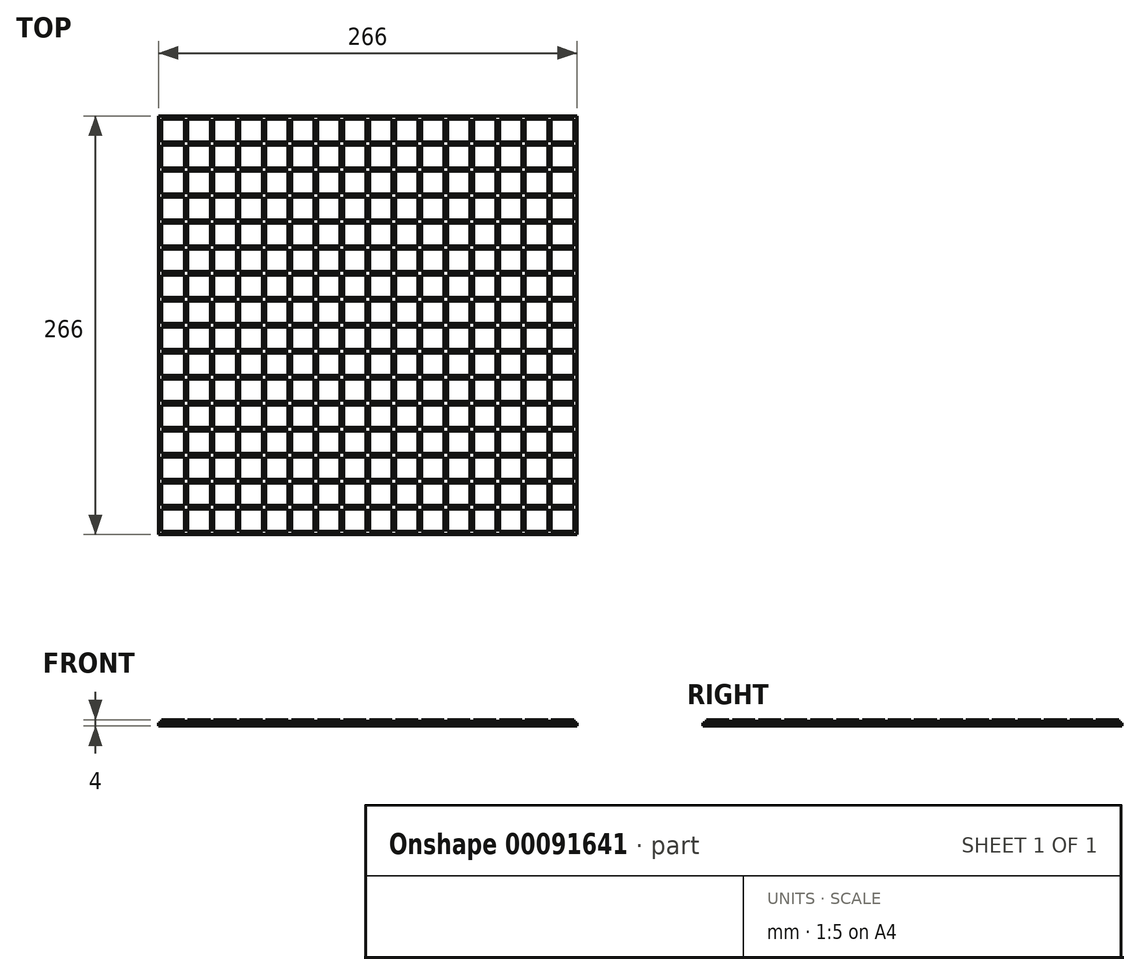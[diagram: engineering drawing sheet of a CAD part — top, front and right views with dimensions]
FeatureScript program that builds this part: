
annotation { "Feature Type Name" : "Feature", "Feature Type Description" : "" }
export const myFeature = defineFeature(function(context is Context, id is Id, definition is map)
    precondition{}
    {
        {
            var Q0;
            Q0=qCreatedBy(makeId("Top.planeOp"),FACE);
            var sketch = newSketch(context, id + "F0", { "sketchPlane" : qUnion([Q0])});
            skLineSegment(sketch, "E0.bottom", {"start": v(133, 133) * mm, "end": v(-133, 133) * mm});
            skLineSegment(sketch, "E0.top", {"start": v(133, -133) * mm, "end": v(-133, -133) * mm});
            skLineSegment(sketch, "E0.left", {"start": v(133, 133) * mm, "end": v(133, -133) * mm});
            skLineSegment(sketch, "E0.right", {"start": v(-133, 133) * mm, "end": v(-133, -133) * mm});
            skPoint(sketch, "E0.middle", {"position": v(0, 0) * mm});
            skSolve(sketch);
        }
        {
            var Q0;
            Q0=qCreatedBy(makeId("Top.planeOp"),FACE);
            var sketch = newSketch(context, id + "F1", { "sketchPlane" : qUnion([Q0])});
            skLineSegment(sketch, "E1.bottom", {"start": v(-116.5, 131) * mm, "end": v(-131, 131) * mm});
            skLineSegment(sketch, "E1.top", {"start": v(-116.5, 116.5) * mm, "end": v(-131, 116.5) * mm});
            skLineSegment(sketch, "E1.left", {"start": v(-116.5, 131) * mm, "end": v(-116.5, 116.5) * mm});
            skLineSegment(sketch, "E1.right", {"start": v(-131, 131) * mm, "end": v(-131, 116.5) * mm});
            skPoint(sketch, "E1.middle", {"position": v(-123.75, 123.75) * mm});
            skPoint(sketch, "E2.0.1.0", {"position": v(-123.75, 107.25) * mm});
            skLineSegment(sketch, "E2.0.1.1", {"start": v(-131, 114.5) * mm, "end": v(-131, 100) * mm});
            skLineSegment(sketch, "E2.0.1.2", {"start": v(-116.5, 114.5) * mm, "end": v(-116.5, 100) * mm});
            skLineSegment(sketch, "E2.0.1.3", {"start": v(-116.5, 100) * mm, "end": v(-131, 100) * mm});
            skLineSegment(sketch, "E2.0.1.4", {"start": v(-116.5, 114.5) * mm, "end": v(-131, 114.5) * mm});
            skPoint(sketch, "E2.0.2.0", {"position": v(-123.75, 90.75) * mm});
            skLineSegment(sketch, "E2.0.2.1", {"start": v(-131, 98) * mm, "end": v(-131, 83.5) * mm});
            skLineSegment(sketch, "E2.0.2.2", {"start": v(-116.5, 98) * mm, "end": v(-116.5, 83.5) * mm});
            skLineSegment(sketch, "E2.0.2.3", {"start": v(-116.5, 83.5) * mm, "end": v(-131, 83.5) * mm});
            skLineSegment(sketch, "E2.0.2.4", {"start": v(-116.5, 98) * mm, "end": v(-131, 98) * mm});
            skPoint(sketch, "E2.0.3.0", {"position": v(-123.75, 74.25) * mm});
            skLineSegment(sketch, "E2.0.3.1", {"start": v(-131, 81.5) * mm, "end": v(-131, 67) * mm});
            skLineSegment(sketch, "E2.0.3.2", {"start": v(-116.5, 81.5) * mm, "end": v(-116.5, 67) * mm});
            skLineSegment(sketch, "E2.0.3.3", {"start": v(-116.5, 67) * mm, "end": v(-131, 67) * mm});
            skLineSegment(sketch, "E2.0.3.4", {"start": v(-116.5, 81.5) * mm, "end": v(-131, 81.5) * mm});
            skPoint(sketch, "E2.0.4.0", {"position": v(-123.75, 57.75) * mm});
            skLineSegment(sketch, "E2.0.4.1", {"start": v(-131, 65) * mm, "end": v(-131, 50.5) * mm});
            skLineSegment(sketch, "E2.0.4.2", {"start": v(-116.5, 65) * mm, "end": v(-116.5, 50.5) * mm});
            skLineSegment(sketch, "E2.0.4.3", {"start": v(-116.5, 50.5) * mm, "end": v(-131, 50.5) * mm});
            skLineSegment(sketch, "E2.0.4.4", {"start": v(-116.5, 65) * mm, "end": v(-131, 65) * mm});
            skPoint(sketch, "E2.0.5.0", {"position": v(-123.75, 41.25) * mm});
            skLineSegment(sketch, "E2.0.5.1", {"start": v(-131, 48.5) * mm, "end": v(-131, 34) * mm});
            skLineSegment(sketch, "E2.0.5.2", {"start": v(-116.5, 48.5) * mm, "end": v(-116.5, 34) * mm});
            skLineSegment(sketch, "E2.0.5.3", {"start": v(-116.5, 34) * mm, "end": v(-131, 34) * mm});
            skLineSegment(sketch, "E2.0.5.4", {"start": v(-116.5, 48.5) * mm, "end": v(-131, 48.5) * mm});
            skPoint(sketch, "E2.0.6.0", {"position": v(-123.75, 24.75) * mm});
            skLineSegment(sketch, "E2.0.6.1", {"start": v(-131, 32) * mm, "end": v(-131, 17.5) * mm});
            skLineSegment(sketch, "E2.0.6.2", {"start": v(-116.5, 32) * mm, "end": v(-116.5, 17.5) * mm});
            skLineSegment(sketch, "E2.0.6.3", {"start": v(-116.5, 17.5) * mm, "end": v(-131, 17.5) * mm});
            skLineSegment(sketch, "E2.0.6.4", {"start": v(-116.5, 32) * mm, "end": v(-131, 32) * mm});
            skPoint(sketch, "E2.0.7.0", {"position": v(-123.75, 8.25) * mm});
            skLineSegment(sketch, "E2.0.7.1", {"start": v(-131, 15.5) * mm, "end": v(-131, 1) * mm});
            skLineSegment(sketch, "E2.0.7.2", {"start": v(-116.5, 15.5) * mm, "end": v(-116.5, 1) * mm});
            skLineSegment(sketch, "E2.0.7.3", {"start": v(-116.5, 1) * mm, "end": v(-131, 1) * mm});
            skLineSegment(sketch, "E2.0.7.4", {"start": v(-116.5, 15.5) * mm, "end": v(-131, 15.5) * mm});
            skPoint(sketch, "E2.0.8.0", {"position": v(-123.75, -8.25) * mm});
            skLineSegment(sketch, "E2.0.8.1", {"start": v(-131, -1) * mm, "end": v(-131, -15.5) * mm});
            skLineSegment(sketch, "E2.0.8.2", {"start": v(-116.5, -1) * mm, "end": v(-116.5, -15.5) * mm});
            skLineSegment(sketch, "E2.0.8.3", {"start": v(-116.5, -15.5) * mm, "end": v(-131, -15.5) * mm});
            skLineSegment(sketch, "E2.0.8.4", {"start": v(-116.5, -1) * mm, "end": v(-131, -1) * mm});
            skPoint(sketch, "E2.0.9.0", {"position": v(-123.75, -24.75) * mm});
            skLineSegment(sketch, "E2.0.9.1", {"start": v(-131, -17.5) * mm, "end": v(-131, -32) * mm});
            skLineSegment(sketch, "E2.0.9.2", {"start": v(-116.5, -17.5) * mm, "end": v(-116.5, -32) * mm});
            skLineSegment(sketch, "E2.0.9.3", {"start": v(-116.5, -32) * mm, "end": v(-131, -32) * mm});
            skLineSegment(sketch, "E2.0.9.4", {"start": v(-116.5, -17.5) * mm, "end": v(-131, -17.5) * mm});
            skPoint(sketch, "E2.0.10.0", {"position": v(-123.75, -41.25) * mm});
            skLineSegment(sketch, "E2.0.10.1", {"start": v(-131, -34) * mm, "end": v(-131, -48.5) * mm});
            skLineSegment(sketch, "E2.0.10.2", {"start": v(-116.5, -34) * mm, "end": v(-116.5, -48.5) * mm});
            skLineSegment(sketch, "E2.0.10.3", {"start": v(-116.5, -48.5) * mm, "end": v(-131, -48.5) * mm});
            skLineSegment(sketch, "E2.0.10.4", {"start": v(-116.5, -34) * mm, "end": v(-131, -34) * mm});
            skPoint(sketch, "E2.0.11.0", {"position": v(-123.75, -57.75) * mm});
            skLineSegment(sketch, "E2.0.11.1", {"start": v(-131, -50.5) * mm, "end": v(-131, -65) * mm});
            skLineSegment(sketch, "E2.0.11.2", {"start": v(-116.5, -50.5) * mm, "end": v(-116.5, -65) * mm});
            skLineSegment(sketch, "E2.0.11.3", {"start": v(-116.5, -65) * mm, "end": v(-131, -65) * mm});
            skLineSegment(sketch, "E2.0.11.4", {"start": v(-116.5, -50.5) * mm, "end": v(-131, -50.5) * mm});
            skPoint(sketch, "E2.0.12.0", {"position": v(-123.75, -74.25) * mm});
            skLineSegment(sketch, "E2.0.12.1", {"start": v(-131, -67) * mm, "end": v(-131, -81.5) * mm});
            skLineSegment(sketch, "E2.0.12.2", {"start": v(-116.5, -67) * mm, "end": v(-116.5, -81.5) * mm});
            skLineSegment(sketch, "E2.0.12.3", {"start": v(-116.5, -81.5) * mm, "end": v(-131, -81.5) * mm});
            skLineSegment(sketch, "E2.0.12.4", {"start": v(-116.5, -67) * mm, "end": v(-131, -67) * mm});
            skPoint(sketch, "E2.0.13.0", {"position": v(-123.75, -90.75) * mm});
            skLineSegment(sketch, "E2.0.13.1", {"start": v(-131, -83.5) * mm, "end": v(-131, -98) * mm});
            skLineSegment(sketch, "E2.0.13.2", {"start": v(-116.5, -83.5) * mm, "end": v(-116.5, -98) * mm});
            skLineSegment(sketch, "E2.0.13.3", {"start": v(-116.5, -98) * mm, "end": v(-131, -98) * mm});
            skLineSegment(sketch, "E2.0.13.4", {"start": v(-116.5, -83.5) * mm, "end": v(-131, -83.5) * mm});
            skPoint(sketch, "E2.0.14.0", {"position": v(-123.75, -107.25) * mm});
            skLineSegment(sketch, "E2.0.14.1", {"start": v(-131, -100) * mm, "end": v(-131, -114.5) * mm});
            skLineSegment(sketch, "E2.0.14.2", {"start": v(-116.5, -100) * mm, "end": v(-116.5, -114.5) * mm});
            skLineSegment(sketch, "E2.0.14.3", {"start": v(-116.5, -114.5) * mm, "end": v(-131, -114.5) * mm});
            skLineSegment(sketch, "E2.0.14.4", {"start": v(-116.5, -100) * mm, "end": v(-131, -100) * mm});
            skPoint(sketch, "E2.0.15.0", {"position": v(-123.75, -123.75) * mm});
            skLineSegment(sketch, "E2.0.15.1", {"start": v(-131, -116.5) * mm, "end": v(-131, -131) * mm});
            skLineSegment(sketch, "E2.0.15.2", {"start": v(-116.5, -116.5) * mm, "end": v(-116.5, -131) * mm});
            skLineSegment(sketch, "E2.0.15.3", {"start": v(-116.5, -131) * mm, "end": v(-131, -131) * mm});
            skLineSegment(sketch, "E2.0.15.4", {"start": v(-116.5, -116.5) * mm, "end": v(-131, -116.5) * mm});
            skPoint(sketch, "E2.1.0.0", {"position": v(-107.25, 123.75) * mm});
            skLineSegment(sketch, "E2.1.0.1", {"start": v(-114.5, 131) * mm, "end": v(-114.5, 116.5) * mm});
            skLineSegment(sketch, "E2.1.0.2", {"start": v(-100, 131) * mm, "end": v(-100, 116.5) * mm});
            skLineSegment(sketch, "E2.1.0.3", {"start": v(-100, 116.5) * mm, "end": v(-114.5, 116.5) * mm});
            skLineSegment(sketch, "E2.1.0.4", {"start": v(-100, 131) * mm, "end": v(-114.5, 131) * mm});
            skPoint(sketch, "E2.1.1.0", {"position": v(-107.25, 107.25) * mm});
            skLineSegment(sketch, "E2.1.1.1", {"start": v(-114.5, 114.5) * mm, "end": v(-114.5, 100) * mm});
            skLineSegment(sketch, "E2.1.1.2", {"start": v(-100, 114.5) * mm, "end": v(-100, 100) * mm});
            skLineSegment(sketch, "E2.1.1.3", {"start": v(-100, 100) * mm, "end": v(-114.5, 100) * mm});
            skLineSegment(sketch, "E2.1.1.4", {"start": v(-100, 114.5) * mm, "end": v(-114.5, 114.5) * mm});
            skPoint(sketch, "E2.1.2.0", {"position": v(-107.25, 90.75) * mm});
            skLineSegment(sketch, "E2.1.2.1", {"start": v(-114.5, 98) * mm, "end": v(-114.5, 83.5) * mm});
            skLineSegment(sketch, "E2.1.2.2", {"start": v(-100, 98) * mm, "end": v(-100, 83.5) * mm});
            skLineSegment(sketch, "E2.1.2.3", {"start": v(-100, 83.5) * mm, "end": v(-114.5, 83.5) * mm});
            skLineSegment(sketch, "E2.1.2.4", {"start": v(-100, 98) * mm, "end": v(-114.5, 98) * mm});
            skPoint(sketch, "E2.1.3.0", {"position": v(-107.25, 74.25) * mm});
            skLineSegment(sketch, "E2.1.3.1", {"start": v(-114.5, 81.5) * mm, "end": v(-114.5, 67) * mm});
            skLineSegment(sketch, "E2.1.3.2", {"start": v(-100, 81.5) * mm, "end": v(-100, 67) * mm});
            skLineSegment(sketch, "E2.1.3.3", {"start": v(-100, 67) * mm, "end": v(-114.5, 67) * mm});
            skLineSegment(sketch, "E2.1.3.4", {"start": v(-100, 81.5) * mm, "end": v(-114.5, 81.5) * mm});
            skPoint(sketch, "E2.1.4.0", {"position": v(-107.25, 57.75) * mm});
            skLineSegment(sketch, "E2.1.4.1", {"start": v(-114.5, 65) * mm, "end": v(-114.5, 50.5) * mm});
            skLineSegment(sketch, "E2.1.4.2", {"start": v(-100, 65) * mm, "end": v(-100, 50.5) * mm});
            skLineSegment(sketch, "E2.1.4.3", {"start": v(-100, 50.5) * mm, "end": v(-114.5, 50.5) * mm});
            skLineSegment(sketch, "E2.1.4.4", {"start": v(-100, 65) * mm, "end": v(-114.5, 65) * mm});
            skPoint(sketch, "E2.1.5.0", {"position": v(-107.25, 41.25) * mm});
            skLineSegment(sketch, "E2.1.5.1", {"start": v(-114.5, 48.5) * mm, "end": v(-114.5, 34) * mm});
            skLineSegment(sketch, "E2.1.5.2", {"start": v(-100, 48.5) * mm, "end": v(-100, 34) * mm});
            skLineSegment(sketch, "E2.1.5.3", {"start": v(-100, 34) * mm, "end": v(-114.5, 34) * mm});
            skLineSegment(sketch, "E2.1.5.4", {"start": v(-100, 48.5) * mm, "end": v(-114.5, 48.5) * mm});
            skPoint(sketch, "E2.1.6.0", {"position": v(-107.25, 24.75) * mm});
            skLineSegment(sketch, "E2.1.6.1", {"start": v(-114.5, 32) * mm, "end": v(-114.5, 17.5) * mm});
            skLineSegment(sketch, "E2.1.6.2", {"start": v(-100, 32) * mm, "end": v(-100, 17.5) * mm});
            skLineSegment(sketch, "E2.1.6.3", {"start": v(-100, 17.5) * mm, "end": v(-114.5, 17.5) * mm});
            skLineSegment(sketch, "E2.1.6.4", {"start": v(-100, 32) * mm, "end": v(-114.5, 32) * mm});
            skPoint(sketch, "E2.1.7.0", {"position": v(-107.25, 8.25) * mm});
            skLineSegment(sketch, "E2.1.7.1", {"start": v(-114.5, 15.5) * mm, "end": v(-114.5, 1) * mm});
            skLineSegment(sketch, "E2.1.7.2", {"start": v(-100, 15.5) * mm, "end": v(-100, 1) * mm});
            skLineSegment(sketch, "E2.1.7.3", {"start": v(-100, 1) * mm, "end": v(-114.5, 1) * mm});
            skLineSegment(sketch, "E2.1.7.4", {"start": v(-100, 15.5) * mm, "end": v(-114.5, 15.5) * mm});
            skPoint(sketch, "E2.1.8.0", {"position": v(-107.25, -8.25) * mm});
            skLineSegment(sketch, "E2.1.8.1", {"start": v(-114.5, -1) * mm, "end": v(-114.5, -15.5) * mm});
            skLineSegment(sketch, "E2.1.8.2", {"start": v(-100, -1) * mm, "end": v(-100, -15.5) * mm});
            skLineSegment(sketch, "E2.1.8.3", {"start": v(-100, -15.5) * mm, "end": v(-114.5, -15.5) * mm});
            skLineSegment(sketch, "E2.1.8.4", {"start": v(-100, -1) * mm, "end": v(-114.5, -1) * mm});
            skPoint(sketch, "E2.1.9.0", {"position": v(-107.25, -24.75) * mm});
            skLineSegment(sketch, "E2.1.9.1", {"start": v(-114.5, -17.5) * mm, "end": v(-114.5, -32) * mm});
            skLineSegment(sketch, "E2.1.9.2", {"start": v(-100, -17.5) * mm, "end": v(-100, -32) * mm});
            skLineSegment(sketch, "E2.1.9.3", {"start": v(-100, -32) * mm, "end": v(-114.5, -32) * mm});
            skLineSegment(sketch, "E2.1.9.4", {"start": v(-100, -17.5) * mm, "end": v(-114.5, -17.5) * mm});
            skPoint(sketch, "E2.1.10.0", {"position": v(-107.25, -41.25) * mm});
            skLineSegment(sketch, "E2.1.10.1", {"start": v(-114.5, -34) * mm, "end": v(-114.5, -48.5) * mm});
            skLineSegment(sketch, "E2.1.10.2", {"start": v(-100, -34) * mm, "end": v(-100, -48.5) * mm});
            skLineSegment(sketch, "E2.1.10.3", {"start": v(-100, -48.5) * mm, "end": v(-114.5, -48.5) * mm});
            skLineSegment(sketch, "E2.1.10.4", {"start": v(-100, -34) * mm, "end": v(-114.5, -34) * mm});
            skPoint(sketch, "E2.1.11.0", {"position": v(-107.25, -57.75) * mm});
            skLineSegment(sketch, "E2.1.11.1", {"start": v(-114.5, -50.5) * mm, "end": v(-114.5, -65) * mm});
            skLineSegment(sketch, "E2.1.11.2", {"start": v(-100, -50.5) * mm, "end": v(-100, -65) * mm});
            skLineSegment(sketch, "E2.1.11.3", {"start": v(-100, -65) * mm, "end": v(-114.5, -65) * mm});
            skLineSegment(sketch, "E2.1.11.4", {"start": v(-100, -50.5) * mm, "end": v(-114.5, -50.5) * mm});
            skPoint(sketch, "E2.1.12.0", {"position": v(-107.25, -74.25) * mm});
            skLineSegment(sketch, "E2.1.12.1", {"start": v(-114.5, -67) * mm, "end": v(-114.5, -81.5) * mm});
            skLineSegment(sketch, "E2.1.12.2", {"start": v(-100, -67) * mm, "end": v(-100, -81.5) * mm});
            skLineSegment(sketch, "E2.1.12.3", {"start": v(-100, -81.5) * mm, "end": v(-114.5, -81.5) * mm});
            skLineSegment(sketch, "E2.1.12.4", {"start": v(-100, -67) * mm, "end": v(-114.5, -67) * mm});
            skPoint(sketch, "E2.1.13.0", {"position": v(-107.25, -90.75) * mm});
            skLineSegment(sketch, "E2.1.13.1", {"start": v(-114.5, -83.5) * mm, "end": v(-114.5, -98) * mm});
            skLineSegment(sketch, "E2.1.13.2", {"start": v(-100, -83.5) * mm, "end": v(-100, -98) * mm});
            skLineSegment(sketch, "E2.1.13.3", {"start": v(-100, -98) * mm, "end": v(-114.5, -98) * mm});
            skLineSegment(sketch, "E2.1.13.4", {"start": v(-100, -83.5) * mm, "end": v(-114.5, -83.5) * mm});
            skPoint(sketch, "E2.1.14.0", {"position": v(-107.25, -107.25) * mm});
            skLineSegment(sketch, "E2.1.14.1", {"start": v(-114.5, -100) * mm, "end": v(-114.5, -114.5) * mm});
            skLineSegment(sketch, "E2.1.14.2", {"start": v(-100, -100) * mm, "end": v(-100, -114.5) * mm});
            skLineSegment(sketch, "E2.1.14.3", {"start": v(-100, -114.5) * mm, "end": v(-114.5, -114.5) * mm});
            skLineSegment(sketch, "E2.1.14.4", {"start": v(-100, -100) * mm, "end": v(-114.5, -100) * mm});
            skPoint(sketch, "E2.1.15.0", {"position": v(-107.25, -123.75) * mm});
            skLineSegment(sketch, "E2.1.15.1", {"start": v(-114.5, -116.5) * mm, "end": v(-114.5, -131) * mm});
            skLineSegment(sketch, "E2.1.15.2", {"start": v(-100, -116.5) * mm, "end": v(-100, -131) * mm});
            skLineSegment(sketch, "E2.1.15.3", {"start": v(-100, -131) * mm, "end": v(-114.5, -131) * mm});
            skLineSegment(sketch, "E2.1.15.4", {"start": v(-100, -116.5) * mm, "end": v(-114.5, -116.5) * mm});
            skPoint(sketch, "E2.2.0.0", {"position": v(-90.75, 123.75) * mm});
            skLineSegment(sketch, "E2.2.0.1", {"start": v(-98, 131) * mm, "end": v(-98, 116.5) * mm});
            skLineSegment(sketch, "E2.2.0.2", {"start": v(-83.5, 131) * mm, "end": v(-83.5, 116.5) * mm});
            skLineSegment(sketch, "E2.2.0.3", {"start": v(-83.5, 116.5) * mm, "end": v(-98, 116.5) * mm});
            skLineSegment(sketch, "E2.2.0.4", {"start": v(-83.5, 131) * mm, "end": v(-98, 131) * mm});
            skPoint(sketch, "E2.2.1.0", {"position": v(-90.75, 107.25) * mm});
            skLineSegment(sketch, "E2.2.1.1", {"start": v(-98, 114.5) * mm, "end": v(-98, 100) * mm});
            skLineSegment(sketch, "E2.2.1.2", {"start": v(-83.5, 114.5) * mm, "end": v(-83.5, 100) * mm});
            skLineSegment(sketch, "E2.2.1.3", {"start": v(-83.5, 100) * mm, "end": v(-98, 100) * mm});
            skLineSegment(sketch, "E2.2.1.4", {"start": v(-83.5, 114.5) * mm, "end": v(-98, 114.5) * mm});
            skPoint(sketch, "E2.2.2.0", {"position": v(-90.75, 90.75) * mm});
            skLineSegment(sketch, "E2.2.2.1", {"start": v(-98, 98) * mm, "end": v(-98, 83.5) * mm});
            skLineSegment(sketch, "E2.2.2.2", {"start": v(-83.5, 98) * mm, "end": v(-83.5, 83.5) * mm});
            skLineSegment(sketch, "E2.2.2.3", {"start": v(-83.5, 83.5) * mm, "end": v(-98, 83.5) * mm});
            skLineSegment(sketch, "E2.2.2.4", {"start": v(-83.5, 98) * mm, "end": v(-98, 98) * mm});
            skPoint(sketch, "E2.2.3.0", {"position": v(-90.75, 74.25) * mm});
            skLineSegment(sketch, "E2.2.3.1", {"start": v(-98, 81.5) * mm, "end": v(-98, 67) * mm});
            skLineSegment(sketch, "E2.2.3.2", {"start": v(-83.5, 81.5) * mm, "end": v(-83.5, 67) * mm});
            skLineSegment(sketch, "E2.2.3.3", {"start": v(-83.5, 67) * mm, "end": v(-98, 67) * mm});
            skLineSegment(sketch, "E2.2.3.4", {"start": v(-83.5, 81.5) * mm, "end": v(-98, 81.5) * mm});
            skPoint(sketch, "E2.2.4.0", {"position": v(-90.75, 57.75) * mm});
            skLineSegment(sketch, "E2.2.4.1", {"start": v(-98, 65) * mm, "end": v(-98, 50.5) * mm});
            skLineSegment(sketch, "E2.2.4.2", {"start": v(-83.5, 65) * mm, "end": v(-83.5, 50.5) * mm});
            skLineSegment(sketch, "E2.2.4.3", {"start": v(-83.5, 50.5) * mm, "end": v(-98, 50.5) * mm});
            skLineSegment(sketch, "E2.2.4.4", {"start": v(-83.5, 65) * mm, "end": v(-98, 65) * mm});
            skPoint(sketch, "E2.2.5.0", {"position": v(-90.75, 41.25) * mm});
            skLineSegment(sketch, "E2.2.5.1", {"start": v(-98, 48.5) * mm, "end": v(-98, 34) * mm});
            skLineSegment(sketch, "E2.2.5.2", {"start": v(-83.5, 48.5) * mm, "end": v(-83.5, 34) * mm});
            skLineSegment(sketch, "E2.2.5.3", {"start": v(-83.5, 34) * mm, "end": v(-98, 34) * mm});
            skLineSegment(sketch, "E2.2.5.4", {"start": v(-83.5, 48.5) * mm, "end": v(-98, 48.5) * mm});
            skPoint(sketch, "E2.2.6.0", {"position": v(-90.75, 24.75) * mm});
            skLineSegment(sketch, "E2.2.6.1", {"start": v(-98, 32) * mm, "end": v(-98, 17.5) * mm});
            skLineSegment(sketch, "E2.2.6.2", {"start": v(-83.5, 32) * mm, "end": v(-83.5, 17.5) * mm});
            skLineSegment(sketch, "E2.2.6.3", {"start": v(-83.5, 17.5) * mm, "end": v(-98, 17.5) * mm});
            skLineSegment(sketch, "E2.2.6.4", {"start": v(-83.5, 32) * mm, "end": v(-98, 32) * mm});
            skPoint(sketch, "E2.2.7.0", {"position": v(-90.75, 8.25) * mm});
            skLineSegment(sketch, "E2.2.7.1", {"start": v(-98, 15.5) * mm, "end": v(-98, 1) * mm});
            skLineSegment(sketch, "E2.2.7.2", {"start": v(-83.5, 15.5) * mm, "end": v(-83.5, 1) * mm});
            skLineSegment(sketch, "E2.2.7.3", {"start": v(-83.5, 1) * mm, "end": v(-98, 1) * mm});
            skLineSegment(sketch, "E2.2.7.4", {"start": v(-83.5, 15.5) * mm, "end": v(-98, 15.5) * mm});
            skPoint(sketch, "E2.2.8.0", {"position": v(-90.75, -8.25) * mm});
            skLineSegment(sketch, "E2.2.8.1", {"start": v(-98, -1) * mm, "end": v(-98, -15.5) * mm});
            skLineSegment(sketch, "E2.2.8.2", {"start": v(-83.5, -1) * mm, "end": v(-83.5, -15.5) * mm});
            skLineSegment(sketch, "E2.2.8.3", {"start": v(-83.5, -15.5) * mm, "end": v(-98, -15.5) * mm});
            skLineSegment(sketch, "E2.2.8.4", {"start": v(-83.5, -1) * mm, "end": v(-98, -1) * mm});
            skPoint(sketch, "E2.2.9.0", {"position": v(-90.75, -24.75) * mm});
            skLineSegment(sketch, "E2.2.9.1", {"start": v(-98, -17.5) * mm, "end": v(-98, -32) * mm});
            skLineSegment(sketch, "E2.2.9.2", {"start": v(-83.5, -17.5) * mm, "end": v(-83.5, -32) * mm});
            skLineSegment(sketch, "E2.2.9.3", {"start": v(-83.5, -32) * mm, "end": v(-98, -32) * mm});
            skLineSegment(sketch, "E2.2.9.4", {"start": v(-83.5, -17.5) * mm, "end": v(-98, -17.5) * mm});
            skPoint(sketch, "E2.2.10.0", {"position": v(-90.75, -41.25) * mm});
            skLineSegment(sketch, "E2.2.10.1", {"start": v(-98, -34) * mm, "end": v(-98, -48.5) * mm});
            skLineSegment(sketch, "E2.2.10.2", {"start": v(-83.5, -34) * mm, "end": v(-83.5, -48.5) * mm});
            skLineSegment(sketch, "E2.2.10.3", {"start": v(-83.5, -48.5) * mm, "end": v(-98, -48.5) * mm});
            skLineSegment(sketch, "E2.2.10.4", {"start": v(-83.5, -34) * mm, "end": v(-98, -34) * mm});
            skPoint(sketch, "E2.2.11.0", {"position": v(-90.75, -57.75) * mm});
            skLineSegment(sketch, "E2.2.11.1", {"start": v(-98, -50.5) * mm, "end": v(-98, -65) * mm});
            skLineSegment(sketch, "E2.2.11.2", {"start": v(-83.5, -50.5) * mm, "end": v(-83.5, -65) * mm});
            skLineSegment(sketch, "E2.2.11.3", {"start": v(-83.5, -65) * mm, "end": v(-98, -65) * mm});
            skLineSegment(sketch, "E2.2.11.4", {"start": v(-83.5, -50.5) * mm, "end": v(-98, -50.5) * mm});
            skPoint(sketch, "E2.2.12.0", {"position": v(-90.75, -74.25) * mm});
            skLineSegment(sketch, "E2.2.12.1", {"start": v(-98, -67) * mm, "end": v(-98, -81.5) * mm});
            skLineSegment(sketch, "E2.2.12.2", {"start": v(-83.5, -67) * mm, "end": v(-83.5, -81.5) * mm});
            skLineSegment(sketch, "E2.2.12.3", {"start": v(-83.5, -81.5) * mm, "end": v(-98, -81.5) * mm});
            skLineSegment(sketch, "E2.2.12.4", {"start": v(-83.5, -67) * mm, "end": v(-98, -67) * mm});
            skPoint(sketch, "E2.2.13.0", {"position": v(-90.75, -90.75) * mm});
            skLineSegment(sketch, "E2.2.13.1", {"start": v(-98, -83.5) * mm, "end": v(-98, -98) * mm});
            skLineSegment(sketch, "E2.2.13.2", {"start": v(-83.5, -83.5) * mm, "end": v(-83.5, -98) * mm});
            skLineSegment(sketch, "E2.2.13.3", {"start": v(-83.5, -98) * mm, "end": v(-98, -98) * mm});
            skLineSegment(sketch, "E2.2.13.4", {"start": v(-83.5, -83.5) * mm, "end": v(-98, -83.5) * mm});
            skPoint(sketch, "E2.2.14.0", {"position": v(-90.75, -107.25) * mm});
            skLineSegment(sketch, "E2.2.14.1", {"start": v(-98, -100) * mm, "end": v(-98, -114.5) * mm});
            skLineSegment(sketch, "E2.2.14.2", {"start": v(-83.5, -100) * mm, "end": v(-83.5, -114.5) * mm});
            skLineSegment(sketch, "E2.2.14.3", {"start": v(-83.5, -114.5) * mm, "end": v(-98, -114.5) * mm});
            skLineSegment(sketch, "E2.2.14.4", {"start": v(-83.5, -100) * mm, "end": v(-98, -100) * mm});
            skPoint(sketch, "E2.2.15.0", {"position": v(-90.75, -123.75) * mm});
            skLineSegment(sketch, "E2.2.15.1", {"start": v(-98, -116.5) * mm, "end": v(-98, -131) * mm});
            skLineSegment(sketch, "E2.2.15.2", {"start": v(-83.5, -116.5) * mm, "end": v(-83.5, -131) * mm});
            skLineSegment(sketch, "E2.2.15.3", {"start": v(-83.5, -131) * mm, "end": v(-98, -131) * mm});
            skLineSegment(sketch, "E2.2.15.4", {"start": v(-83.5, -116.5) * mm, "end": v(-98, -116.5) * mm});
            skPoint(sketch, "E2.3.0.0", {"position": v(-74.25, 123.75) * mm});
            skLineSegment(sketch, "E2.3.0.1", {"start": v(-81.5, 131) * mm, "end": v(-81.5, 116.5) * mm});
            skLineSegment(sketch, "E2.3.0.2", {"start": v(-67, 131) * mm, "end": v(-67, 116.5) * mm});
            skLineSegment(sketch, "E2.3.0.3", {"start": v(-67, 116.5) * mm, "end": v(-81.5, 116.5) * mm});
            skLineSegment(sketch, "E2.3.0.4", {"start": v(-67, 131) * mm, "end": v(-81.5, 131) * mm});
            skPoint(sketch, "E2.3.1.0", {"position": v(-74.25, 107.25) * mm});
            skLineSegment(sketch, "E2.3.1.1", {"start": v(-81.5, 114.5) * mm, "end": v(-81.5, 100) * mm});
            skLineSegment(sketch, "E2.3.1.2", {"start": v(-67, 114.5) * mm, "end": v(-67, 100) * mm});
            skLineSegment(sketch, "E2.3.1.3", {"start": v(-67, 100) * mm, "end": v(-81.5, 100) * mm});
            skLineSegment(sketch, "E2.3.1.4", {"start": v(-67, 114.5) * mm, "end": v(-81.5, 114.5) * mm});
            skPoint(sketch, "E2.3.2.0", {"position": v(-74.25, 90.75) * mm});
            skLineSegment(sketch, "E2.3.2.1", {"start": v(-81.5, 98) * mm, "end": v(-81.5, 83.5) * mm});
            skLineSegment(sketch, "E2.3.2.2", {"start": v(-67, 98) * mm, "end": v(-67, 83.5) * mm});
            skLineSegment(sketch, "E2.3.2.3", {"start": v(-67, 83.5) * mm, "end": v(-81.5, 83.5) * mm});
            skLineSegment(sketch, "E2.3.2.4", {"start": v(-67, 98) * mm, "end": v(-81.5, 98) * mm});
            skPoint(sketch, "E2.3.3.0", {"position": v(-74.25, 74.25) * mm});
            skLineSegment(sketch, "E2.3.3.1", {"start": v(-81.5, 81.5) * mm, "end": v(-81.5, 67) * mm});
            skLineSegment(sketch, "E2.3.3.2", {"start": v(-67, 81.5) * mm, "end": v(-67, 67) * mm});
            skLineSegment(sketch, "E2.3.3.3", {"start": v(-67, 67) * mm, "end": v(-81.5, 67) * mm});
            skLineSegment(sketch, "E2.3.3.4", {"start": v(-67, 81.5) * mm, "end": v(-81.5, 81.5) * mm});
            skPoint(sketch, "E2.3.4.0", {"position": v(-74.25, 57.75) * mm});
            skLineSegment(sketch, "E2.3.4.1", {"start": v(-81.5, 65) * mm, "end": v(-81.5, 50.5) * mm});
            skLineSegment(sketch, "E2.3.4.2", {"start": v(-67, 65) * mm, "end": v(-67, 50.5) * mm});
            skLineSegment(sketch, "E2.3.4.3", {"start": v(-67, 50.5) * mm, "end": v(-81.5, 50.5) * mm});
            skLineSegment(sketch, "E2.3.4.4", {"start": v(-67, 65) * mm, "end": v(-81.5, 65) * mm});
            skPoint(sketch, "E2.3.5.0", {"position": v(-74.25, 41.25) * mm});
            skLineSegment(sketch, "E2.3.5.1", {"start": v(-81.5, 48.5) * mm, "end": v(-81.5, 34) * mm});
            skLineSegment(sketch, "E2.3.5.2", {"start": v(-67, 48.5) * mm, "end": v(-67, 34) * mm});
            skLineSegment(sketch, "E2.3.5.3", {"start": v(-67, 34) * mm, "end": v(-81.5, 34) * mm});
            skLineSegment(sketch, "E2.3.5.4", {"start": v(-67, 48.5) * mm, "end": v(-81.5, 48.5) * mm});
            skPoint(sketch, "E2.3.6.0", {"position": v(-74.25, 24.75) * mm});
            skLineSegment(sketch, "E2.3.6.1", {"start": v(-81.5, 32) * mm, "end": v(-81.5, 17.5) * mm});
            skLineSegment(sketch, "E2.3.6.2", {"start": v(-67, 32) * mm, "end": v(-67, 17.5) * mm});
            skLineSegment(sketch, "E2.3.6.3", {"start": v(-67, 17.5) * mm, "end": v(-81.5, 17.5) * mm});
            skLineSegment(sketch, "E2.3.6.4", {"start": v(-67, 32) * mm, "end": v(-81.5, 32) * mm});
            skPoint(sketch, "E2.3.7.0", {"position": v(-74.25, 8.25) * mm});
            skLineSegment(sketch, "E2.3.7.1", {"start": v(-81.5, 15.5) * mm, "end": v(-81.5, 1) * mm});
            skLineSegment(sketch, "E2.3.7.2", {"start": v(-67, 15.5) * mm, "end": v(-67, 1) * mm});
            skLineSegment(sketch, "E2.3.7.3", {"start": v(-67, 1) * mm, "end": v(-81.5, 1) * mm});
            skLineSegment(sketch, "E2.3.7.4", {"start": v(-67, 15.5) * mm, "end": v(-81.5, 15.5) * mm});
            skPoint(sketch, "E2.3.8.0", {"position": v(-74.25, -8.25) * mm});
            skLineSegment(sketch, "E2.3.8.1", {"start": v(-81.5, -1) * mm, "end": v(-81.5, -15.5) * mm});
            skLineSegment(sketch, "E2.3.8.2", {"start": v(-67, -1) * mm, "end": v(-67, -15.5) * mm});
            skLineSegment(sketch, "E2.3.8.3", {"start": v(-67, -15.5) * mm, "end": v(-81.5, -15.5) * mm});
            skLineSegment(sketch, "E2.3.8.4", {"start": v(-67, -1) * mm, "end": v(-81.5, -1) * mm});
            skPoint(sketch, "E2.3.9.0", {"position": v(-74.25, -24.75) * mm});
            skLineSegment(sketch, "E2.3.9.1", {"start": v(-81.5, -17.5) * mm, "end": v(-81.5, -32) * mm});
            skLineSegment(sketch, "E2.3.9.2", {"start": v(-67, -17.5) * mm, "end": v(-67, -32) * mm});
            skLineSegment(sketch, "E2.3.9.3", {"start": v(-67, -32) * mm, "end": v(-81.5, -32) * mm});
            skLineSegment(sketch, "E2.3.9.4", {"start": v(-67, -17.5) * mm, "end": v(-81.5, -17.5) * mm});
            skPoint(sketch, "E2.3.10.0", {"position": v(-74.25, -41.25) * mm});
            skLineSegment(sketch, "E2.3.10.1", {"start": v(-81.5, -34) * mm, "end": v(-81.5, -48.5) * mm});
            skLineSegment(sketch, "E2.3.10.2", {"start": v(-67, -34) * mm, "end": v(-67, -48.5) * mm});
            skLineSegment(sketch, "E2.3.10.3", {"start": v(-67, -48.5) * mm, "end": v(-81.5, -48.5) * mm});
            skLineSegment(sketch, "E2.3.10.4", {"start": v(-67, -34) * mm, "end": v(-81.5, -34) * mm});
            skPoint(sketch, "E2.3.11.0", {"position": v(-74.25, -57.75) * mm});
            skLineSegment(sketch, "E2.3.11.1", {"start": v(-81.5, -50.5) * mm, "end": v(-81.5, -65) * mm});
            skLineSegment(sketch, "E2.3.11.2", {"start": v(-67, -50.5) * mm, "end": v(-67, -65) * mm});
            skLineSegment(sketch, "E2.3.11.3", {"start": v(-67, -65) * mm, "end": v(-81.5, -65) * mm});
            skLineSegment(sketch, "E2.3.11.4", {"start": v(-67, -50.5) * mm, "end": v(-81.5, -50.5) * mm});
            skPoint(sketch, "E2.3.12.0", {"position": v(-74.25, -74.25) * mm});
            skLineSegment(sketch, "E2.3.12.1", {"start": v(-81.5, -67) * mm, "end": v(-81.5, -81.5) * mm});
            skLineSegment(sketch, "E2.3.12.2", {"start": v(-67, -67) * mm, "end": v(-67, -81.5) * mm});
            skLineSegment(sketch, "E2.3.12.3", {"start": v(-67, -81.5) * mm, "end": v(-81.5, -81.5) * mm});
            skLineSegment(sketch, "E2.3.12.4", {"start": v(-67, -67) * mm, "end": v(-81.5, -67) * mm});
            skPoint(sketch, "E2.3.13.0", {"position": v(-74.25, -90.75) * mm});
            skLineSegment(sketch, "E2.3.13.1", {"start": v(-81.5, -83.5) * mm, "end": v(-81.5, -98) * mm});
            skLineSegment(sketch, "E2.3.13.2", {"start": v(-67, -83.5) * mm, "end": v(-67, -98) * mm});
            skLineSegment(sketch, "E2.3.13.3", {"start": v(-67, -98) * mm, "end": v(-81.5, -98) * mm});
            skLineSegment(sketch, "E2.3.13.4", {"start": v(-67, -83.5) * mm, "end": v(-81.5, -83.5) * mm});
            skPoint(sketch, "E2.3.14.0", {"position": v(-74.25, -107.25) * mm});
            skLineSegment(sketch, "E2.3.14.1", {"start": v(-81.5, -100) * mm, "end": v(-81.5, -114.5) * mm});
            skLineSegment(sketch, "E2.3.14.2", {"start": v(-67, -100) * mm, "end": v(-67, -114.5) * mm});
            skLineSegment(sketch, "E2.3.14.3", {"start": v(-67, -114.5) * mm, "end": v(-81.5, -114.5) * mm});
            skLineSegment(sketch, "E2.3.14.4", {"start": v(-67, -100) * mm, "end": v(-81.5, -100) * mm});
            skPoint(sketch, "E2.3.15.0", {"position": v(-74.25, -123.75) * mm});
            skLineSegment(sketch, "E2.3.15.1", {"start": v(-81.5, -116.5) * mm, "end": v(-81.5, -131) * mm});
            skLineSegment(sketch, "E2.3.15.2", {"start": v(-67, -116.5) * mm, "end": v(-67, -131) * mm});
            skLineSegment(sketch, "E2.3.15.3", {"start": v(-67, -131) * mm, "end": v(-81.5, -131) * mm});
            skLineSegment(sketch, "E2.3.15.4", {"start": v(-67, -116.5) * mm, "end": v(-81.5, -116.5) * mm});
            skPoint(sketch, "E2.4.0.0", {"position": v(-57.75, 123.75) * mm});
            skLineSegment(sketch, "E2.4.0.1", {"start": v(-65, 131) * mm, "end": v(-65, 116.5) * mm});
            skLineSegment(sketch, "E2.4.0.2", {"start": v(-50.5, 131) * mm, "end": v(-50.5, 116.5) * mm});
            skLineSegment(sketch, "E2.4.0.3", {"start": v(-50.5, 116.5) * mm, "end": v(-65, 116.5) * mm});
            skLineSegment(sketch, "E2.4.0.4", {"start": v(-50.5, 131) * mm, "end": v(-65, 131) * mm});
            skPoint(sketch, "E2.4.1.0", {"position": v(-57.75, 107.25) * mm});
            skLineSegment(sketch, "E2.4.1.1", {"start": v(-65, 114.5) * mm, "end": v(-65, 100) * mm});
            skLineSegment(sketch, "E2.4.1.2", {"start": v(-50.5, 114.5) * mm, "end": v(-50.5, 100) * mm});
            skLineSegment(sketch, "E2.4.1.3", {"start": v(-50.5, 100) * mm, "end": v(-65, 100) * mm});
            skLineSegment(sketch, "E2.4.1.4", {"start": v(-50.5, 114.5) * mm, "end": v(-65, 114.5) * mm});
            skPoint(sketch, "E2.4.2.0", {"position": v(-57.75, 90.75) * mm});
            skLineSegment(sketch, "E2.4.2.1", {"start": v(-65, 98) * mm, "end": v(-65, 83.5) * mm});
            skLineSegment(sketch, "E2.4.2.2", {"start": v(-50.5, 98) * mm, "end": v(-50.5, 83.5) * mm});
            skLineSegment(sketch, "E2.4.2.3", {"start": v(-50.5, 83.5) * mm, "end": v(-65, 83.5) * mm});
            skLineSegment(sketch, "E2.4.2.4", {"start": v(-50.5, 98) * mm, "end": v(-65, 98) * mm});
            skPoint(sketch, "E2.4.3.0", {"position": v(-57.75, 74.25) * mm});
            skLineSegment(sketch, "E2.4.3.1", {"start": v(-65, 81.5) * mm, "end": v(-65, 67) * mm});
            skLineSegment(sketch, "E2.4.3.2", {"start": v(-50.5, 81.5) * mm, "end": v(-50.5, 67) * mm});
            skLineSegment(sketch, "E2.4.3.3", {"start": v(-50.5, 67) * mm, "end": v(-65, 67) * mm});
            skLineSegment(sketch, "E2.4.3.4", {"start": v(-50.5, 81.5) * mm, "end": v(-65, 81.5) * mm});
            skPoint(sketch, "E2.4.4.0", {"position": v(-57.75, 57.75) * mm});
            skLineSegment(sketch, "E2.4.4.1", {"start": v(-65, 65) * mm, "end": v(-65, 50.5) * mm});
            skLineSegment(sketch, "E2.4.4.2", {"start": v(-50.5, 65) * mm, "end": v(-50.5, 50.5) * mm});
            skLineSegment(sketch, "E2.4.4.3", {"start": v(-50.5, 50.5) * mm, "end": v(-65, 50.5) * mm});
            skLineSegment(sketch, "E2.4.4.4", {"start": v(-50.5, 65) * mm, "end": v(-65, 65) * mm});
            skPoint(sketch, "E2.4.5.0", {"position": v(-57.75, 41.25) * mm});
            skLineSegment(sketch, "E2.4.5.1", {"start": v(-65, 48.5) * mm, "end": v(-65, 34) * mm});
            skLineSegment(sketch, "E2.4.5.2", {"start": v(-50.5, 48.5) * mm, "end": v(-50.5, 34) * mm});
            skLineSegment(sketch, "E2.4.5.3", {"start": v(-50.5, 34) * mm, "end": v(-65, 34) * mm});
            skLineSegment(sketch, "E2.4.5.4", {"start": v(-50.5, 48.5) * mm, "end": v(-65, 48.5) * mm});
            skPoint(sketch, "E2.4.6.0", {"position": v(-57.75, 24.75) * mm});
            skLineSegment(sketch, "E2.4.6.1", {"start": v(-65, 32) * mm, "end": v(-65, 17.5) * mm});
            skLineSegment(sketch, "E2.4.6.2", {"start": v(-50.5, 32) * mm, "end": v(-50.5, 17.5) * mm});
            skLineSegment(sketch, "E2.4.6.3", {"start": v(-50.5, 17.5) * mm, "end": v(-65, 17.5) * mm});
            skLineSegment(sketch, "E2.4.6.4", {"start": v(-50.5, 32) * mm, "end": v(-65, 32) * mm});
            skPoint(sketch, "E2.4.7.0", {"position": v(-57.75, 8.25) * mm});
            skLineSegment(sketch, "E2.4.7.1", {"start": v(-65, 15.5) * mm, "end": v(-65, 1) * mm});
            skLineSegment(sketch, "E2.4.7.2", {"start": v(-50.5, 15.5) * mm, "end": v(-50.5, 1) * mm});
            skLineSegment(sketch, "E2.4.7.3", {"start": v(-50.5, 1) * mm, "end": v(-65, 1) * mm});
            skLineSegment(sketch, "E2.4.7.4", {"start": v(-50.5, 15.5) * mm, "end": v(-65, 15.5) * mm});
            skPoint(sketch, "E2.4.8.0", {"position": v(-57.75, -8.25) * mm});
            skLineSegment(sketch, "E2.4.8.1", {"start": v(-65, -1) * mm, "end": v(-65, -15.5) * mm});
            skLineSegment(sketch, "E2.4.8.2", {"start": v(-50.5, -1) * mm, "end": v(-50.5, -15.5) * mm});
            skLineSegment(sketch, "E2.4.8.3", {"start": v(-50.5, -15.5) * mm, "end": v(-65, -15.5) * mm});
            skLineSegment(sketch, "E2.4.8.4", {"start": v(-50.5, -1) * mm, "end": v(-65, -1) * mm});
            skPoint(sketch, "E2.4.9.0", {"position": v(-57.75, -24.75) * mm});
            skLineSegment(sketch, "E2.4.9.1", {"start": v(-65, -17.5) * mm, "end": v(-65, -32) * mm});
            skLineSegment(sketch, "E2.4.9.2", {"start": v(-50.5, -17.5) * mm, "end": v(-50.5, -32) * mm});
            skLineSegment(sketch, "E2.4.9.3", {"start": v(-50.5, -32) * mm, "end": v(-65, -32) * mm});
            skLineSegment(sketch, "E2.4.9.4", {"start": v(-50.5, -17.5) * mm, "end": v(-65, -17.5) * mm});
            skPoint(sketch, "E2.4.10.0", {"position": v(-57.75, -41.25) * mm});
            skLineSegment(sketch, "E2.4.10.1", {"start": v(-65, -34) * mm, "end": v(-65, -48.5) * mm});
            skLineSegment(sketch, "E2.4.10.2", {"start": v(-50.5, -34) * mm, "end": v(-50.5, -48.5) * mm});
            skLineSegment(sketch, "E2.4.10.3", {"start": v(-50.5, -48.5) * mm, "end": v(-65, -48.5) * mm});
            skLineSegment(sketch, "E2.4.10.4", {"start": v(-50.5, -34) * mm, "end": v(-65, -34) * mm});
            skPoint(sketch, "E2.4.11.0", {"position": v(-57.75, -57.75) * mm});
            skLineSegment(sketch, "E2.4.11.1", {"start": v(-65, -50.5) * mm, "end": v(-65, -65) * mm});
            skLineSegment(sketch, "E2.4.11.2", {"start": v(-50.5, -50.5) * mm, "end": v(-50.5, -65) * mm});
            skLineSegment(sketch, "E2.4.11.3", {"start": v(-50.5, -65) * mm, "end": v(-65, -65) * mm});
            skLineSegment(sketch, "E2.4.11.4", {"start": v(-50.5, -50.5) * mm, "end": v(-65, -50.5) * mm});
            skPoint(sketch, "E2.4.12.0", {"position": v(-57.75, -74.25) * mm});
            skLineSegment(sketch, "E2.4.12.1", {"start": v(-65, -67) * mm, "end": v(-65, -81.5) * mm});
            skLineSegment(sketch, "E2.4.12.2", {"start": v(-50.5, -67) * mm, "end": v(-50.5, -81.5) * mm});
            skLineSegment(sketch, "E2.4.12.3", {"start": v(-50.5, -81.5) * mm, "end": v(-65, -81.5) * mm});
            skLineSegment(sketch, "E2.4.12.4", {"start": v(-50.5, -67) * mm, "end": v(-65, -67) * mm});
            skPoint(sketch, "E2.4.13.0", {"position": v(-57.75, -90.75) * mm});
            skLineSegment(sketch, "E2.4.13.1", {"start": v(-65, -83.5) * mm, "end": v(-65, -98) * mm});
            skLineSegment(sketch, "E2.4.13.2", {"start": v(-50.5, -83.5) * mm, "end": v(-50.5, -98) * mm});
            skLineSegment(sketch, "E2.4.13.3", {"start": v(-50.5, -98) * mm, "end": v(-65, -98) * mm});
            skLineSegment(sketch, "E2.4.13.4", {"start": v(-50.5, -83.5) * mm, "end": v(-65, -83.5) * mm});
            skPoint(sketch, "E2.4.14.0", {"position": v(-57.75, -107.25) * mm});
            skLineSegment(sketch, "E2.4.14.1", {"start": v(-65, -100) * mm, "end": v(-65, -114.5) * mm});
            skLineSegment(sketch, "E2.4.14.2", {"start": v(-50.5, -100) * mm, "end": v(-50.5, -114.5) * mm});
            skLineSegment(sketch, "E2.4.14.3", {"start": v(-50.5, -114.5) * mm, "end": v(-65, -114.5) * mm});
            skLineSegment(sketch, "E2.4.14.4", {"start": v(-50.5, -100) * mm, "end": v(-65, -100) * mm});
            skPoint(sketch, "E2.4.15.0", {"position": v(-57.75, -123.75) * mm});
            skLineSegment(sketch, "E2.4.15.1", {"start": v(-65, -116.5) * mm, "end": v(-65, -131) * mm});
            skLineSegment(sketch, "E2.4.15.2", {"start": v(-50.5, -116.5) * mm, "end": v(-50.5, -131) * mm});
            skLineSegment(sketch, "E2.4.15.3", {"start": v(-50.5, -131) * mm, "end": v(-65, -131) * mm});
            skLineSegment(sketch, "E2.4.15.4", {"start": v(-50.5, -116.5) * mm, "end": v(-65, -116.5) * mm});
            skPoint(sketch, "E2.5.0.0", {"position": v(-41.25, 123.75) * mm});
            skLineSegment(sketch, "E2.5.0.1", {"start": v(-48.5, 131) * mm, "end": v(-48.5, 116.5) * mm});
            skLineSegment(sketch, "E2.5.0.2", {"start": v(-34, 131) * mm, "end": v(-34, 116.5) * mm});
            skLineSegment(sketch, "E2.5.0.3", {"start": v(-34, 116.5) * mm, "end": v(-48.5, 116.5) * mm});
            skLineSegment(sketch, "E2.5.0.4", {"start": v(-34, 131) * mm, "end": v(-48.5, 131) * mm});
            skPoint(sketch, "E2.5.1.0", {"position": v(-41.25, 107.25) * mm});
            skLineSegment(sketch, "E2.5.1.1", {"start": v(-48.5, 114.5) * mm, "end": v(-48.5, 100) * mm});
            skLineSegment(sketch, "E2.5.1.2", {"start": v(-34, 114.5) * mm, "end": v(-34, 100) * mm});
            skLineSegment(sketch, "E2.5.1.3", {"start": v(-34, 100) * mm, "end": v(-48.5, 100) * mm});
            skLineSegment(sketch, "E2.5.1.4", {"start": v(-34, 114.5) * mm, "end": v(-48.5, 114.5) * mm});
            skPoint(sketch, "E2.5.2.0", {"position": v(-41.25, 90.75) * mm});
            skLineSegment(sketch, "E2.5.2.1", {"start": v(-48.5, 98) * mm, "end": v(-48.5, 83.5) * mm});
            skLineSegment(sketch, "E2.5.2.2", {"start": v(-34, 98) * mm, "end": v(-34, 83.5) * mm});
            skLineSegment(sketch, "E2.5.2.3", {"start": v(-34, 83.5) * mm, "end": v(-48.5, 83.5) * mm});
            skLineSegment(sketch, "E2.5.2.4", {"start": v(-34, 98) * mm, "end": v(-48.5, 98) * mm});
            skPoint(sketch, "E2.5.3.0", {"position": v(-41.25, 74.25) * mm});
            skLineSegment(sketch, "E2.5.3.1", {"start": v(-48.5, 81.5) * mm, "end": v(-48.5, 67) * mm});
            skLineSegment(sketch, "E2.5.3.2", {"start": v(-34, 81.5) * mm, "end": v(-34, 67) * mm});
            skLineSegment(sketch, "E2.5.3.3", {"start": v(-34, 67) * mm, "end": v(-48.5, 67) * mm});
            skLineSegment(sketch, "E2.5.3.4", {"start": v(-34, 81.5) * mm, "end": v(-48.5, 81.5) * mm});
            skPoint(sketch, "E2.5.4.0", {"position": v(-41.25, 57.75) * mm});
            skLineSegment(sketch, "E2.5.4.1", {"start": v(-48.5, 65) * mm, "end": v(-48.5, 50.5) * mm});
            skLineSegment(sketch, "E2.5.4.2", {"start": v(-34, 65) * mm, "end": v(-34, 50.5) * mm});
            skLineSegment(sketch, "E2.5.4.3", {"start": v(-34, 50.5) * mm, "end": v(-48.5, 50.5) * mm});
            skLineSegment(sketch, "E2.5.4.4", {"start": v(-34, 65) * mm, "end": v(-48.5, 65) * mm});
            skPoint(sketch, "E2.5.5.0", {"position": v(-41.25, 41.25) * mm});
            skLineSegment(sketch, "E2.5.5.1", {"start": v(-48.5, 48.5) * mm, "end": v(-48.5, 34) * mm});
            skLineSegment(sketch, "E2.5.5.2", {"start": v(-34, 48.5) * mm, "end": v(-34, 34) * mm});
            skLineSegment(sketch, "E2.5.5.3", {"start": v(-34, 34) * mm, "end": v(-48.5, 34) * mm});
            skLineSegment(sketch, "E2.5.5.4", {"start": v(-34, 48.5) * mm, "end": v(-48.5, 48.5) * mm});
            skPoint(sketch, "E2.5.6.0", {"position": v(-41.25, 24.75) * mm});
            skLineSegment(sketch, "E2.5.6.1", {"start": v(-48.5, 32) * mm, "end": v(-48.5, 17.5) * mm});
            skLineSegment(sketch, "E2.5.6.2", {"start": v(-34, 32) * mm, "end": v(-34, 17.5) * mm});
            skLineSegment(sketch, "E2.5.6.3", {"start": v(-34, 17.5) * mm, "end": v(-48.5, 17.5) * mm});
            skLineSegment(sketch, "E2.5.6.4", {"start": v(-34, 32) * mm, "end": v(-48.5, 32) * mm});
            skPoint(sketch, "E2.5.7.0", {"position": v(-41.25, 8.25) * mm});
            skLineSegment(sketch, "E2.5.7.1", {"start": v(-48.5, 15.5) * mm, "end": v(-48.5, 1) * mm});
            skLineSegment(sketch, "E2.5.7.2", {"start": v(-34, 15.5) * mm, "end": v(-34, 1) * mm});
            skLineSegment(sketch, "E2.5.7.3", {"start": v(-34, 1) * mm, "end": v(-48.5, 1) * mm});
            skLineSegment(sketch, "E2.5.7.4", {"start": v(-34, 15.5) * mm, "end": v(-48.5, 15.5) * mm});
            skPoint(sketch, "E2.5.8.0", {"position": v(-41.25, -8.25) * mm});
            skLineSegment(sketch, "E2.5.8.1", {"start": v(-48.5, -1) * mm, "end": v(-48.5, -15.5) * mm});
            skLineSegment(sketch, "E2.5.8.2", {"start": v(-34, -1) * mm, "end": v(-34, -15.5) * mm});
            skLineSegment(sketch, "E2.5.8.3", {"start": v(-34, -15.5) * mm, "end": v(-48.5, -15.5) * mm});
            skLineSegment(sketch, "E2.5.8.4", {"start": v(-34, -1) * mm, "end": v(-48.5, -1) * mm});
            skPoint(sketch, "E2.5.9.0", {"position": v(-41.25, -24.75) * mm});
            skLineSegment(sketch, "E2.5.9.1", {"start": v(-48.5, -17.5) * mm, "end": v(-48.5, -32) * mm});
            skLineSegment(sketch, "E2.5.9.2", {"start": v(-34, -17.5) * mm, "end": v(-34, -32) * mm});
            skLineSegment(sketch, "E2.5.9.3", {"start": v(-34, -32) * mm, "end": v(-48.5, -32) * mm});
            skLineSegment(sketch, "E2.5.9.4", {"start": v(-34, -17.5) * mm, "end": v(-48.5, -17.5) * mm});
            skPoint(sketch, "E2.5.10.0", {"position": v(-41.25, -41.25) * mm});
            skLineSegment(sketch, "E2.5.10.1", {"start": v(-48.5, -34) * mm, "end": v(-48.5, -48.5) * mm});
            skLineSegment(sketch, "E2.5.10.2", {"start": v(-34, -34) * mm, "end": v(-34, -48.5) * mm});
            skLineSegment(sketch, "E2.5.10.3", {"start": v(-34, -48.5) * mm, "end": v(-48.5, -48.5) * mm});
            skLineSegment(sketch, "E2.5.10.4", {"start": v(-34, -34) * mm, "end": v(-48.5, -34) * mm});
            skPoint(sketch, "E2.5.11.0", {"position": v(-41.25, -57.75) * mm});
            skLineSegment(sketch, "E2.5.11.1", {"start": v(-48.5, -50.5) * mm, "end": v(-48.5, -65) * mm});
            skLineSegment(sketch, "E2.5.11.2", {"start": v(-34, -50.5) * mm, "end": v(-34, -65) * mm});
            skLineSegment(sketch, "E2.5.11.3", {"start": v(-34, -65) * mm, "end": v(-48.5, -65) * mm});
            skLineSegment(sketch, "E2.5.11.4", {"start": v(-34, -50.5) * mm, "end": v(-48.5, -50.5) * mm});
            skPoint(sketch, "E2.5.12.0", {"position": v(-41.25, -74.25) * mm});
            skLineSegment(sketch, "E2.5.12.1", {"start": v(-48.5, -67) * mm, "end": v(-48.5, -81.5) * mm});
            skLineSegment(sketch, "E2.5.12.2", {"start": v(-34, -67) * mm, "end": v(-34, -81.5) * mm});
            skLineSegment(sketch, "E2.5.12.3", {"start": v(-34, -81.5) * mm, "end": v(-48.5, -81.5) * mm});
            skLineSegment(sketch, "E2.5.12.4", {"start": v(-34, -67) * mm, "end": v(-48.5, -67) * mm});
            skPoint(sketch, "E2.5.13.0", {"position": v(-41.25, -90.75) * mm});
            skLineSegment(sketch, "E2.5.13.1", {"start": v(-48.5, -83.5) * mm, "end": v(-48.5, -98) * mm});
            skLineSegment(sketch, "E2.5.13.2", {"start": v(-34, -83.5) * mm, "end": v(-34, -98) * mm});
            skLineSegment(sketch, "E2.5.13.3", {"start": v(-34, -98) * mm, "end": v(-48.5, -98) * mm});
            skLineSegment(sketch, "E2.5.13.4", {"start": v(-34, -83.5) * mm, "end": v(-48.5, -83.5) * mm});
            skPoint(sketch, "E2.5.14.0", {"position": v(-41.25, -107.25) * mm});
            skLineSegment(sketch, "E2.5.14.1", {"start": v(-48.5, -100) * mm, "end": v(-48.5, -114.5) * mm});
            skLineSegment(sketch, "E2.5.14.2", {"start": v(-34, -100) * mm, "end": v(-34, -114.5) * mm});
            skLineSegment(sketch, "E2.5.14.3", {"start": v(-34, -114.5) * mm, "end": v(-48.5, -114.5) * mm});
            skLineSegment(sketch, "E2.5.14.4", {"start": v(-34, -100) * mm, "end": v(-48.5, -100) * mm});
            skPoint(sketch, "E2.5.15.0", {"position": v(-41.25, -123.75) * mm});
            skLineSegment(sketch, "E2.5.15.1", {"start": v(-48.5, -116.5) * mm, "end": v(-48.5, -131) * mm});
            skLineSegment(sketch, "E2.5.15.2", {"start": v(-34, -116.5) * mm, "end": v(-34, -131) * mm});
            skLineSegment(sketch, "E2.5.15.3", {"start": v(-34, -131) * mm, "end": v(-48.5, -131) * mm});
            skLineSegment(sketch, "E2.5.15.4", {"start": v(-34, -116.5) * mm, "end": v(-48.5, -116.5) * mm});
            skPoint(sketch, "E2.6.0.0", {"position": v(-24.75, 123.75) * mm});
            skLineSegment(sketch, "E2.6.0.1", {"start": v(-32, 131) * mm, "end": v(-32, 116.5) * mm});
            skLineSegment(sketch, "E2.6.0.2", {"start": v(-17.5, 131) * mm, "end": v(-17.5, 116.5) * mm});
            skLineSegment(sketch, "E2.6.0.3", {"start": v(-17.5, 116.5) * mm, "end": v(-32, 116.5) * mm});
            skLineSegment(sketch, "E2.6.0.4", {"start": v(-17.5, 131) * mm, "end": v(-32, 131) * mm});
            skPoint(sketch, "E2.6.1.0", {"position": v(-24.75, 107.25) * mm});
            skLineSegment(sketch, "E2.6.1.1", {"start": v(-32, 114.5) * mm, "end": v(-32, 100) * mm});
            skLineSegment(sketch, "E2.6.1.2", {"start": v(-17.5, 114.5) * mm, "end": v(-17.5, 100) * mm});
            skLineSegment(sketch, "E2.6.1.3", {"start": v(-17.5, 100) * mm, "end": v(-32, 100) * mm});
            skLineSegment(sketch, "E2.6.1.4", {"start": v(-17.5, 114.5) * mm, "end": v(-32, 114.5) * mm});
            skPoint(sketch, "E2.6.2.0", {"position": v(-24.75, 90.75) * mm});
            skLineSegment(sketch, "E2.6.2.1", {"start": v(-32, 98) * mm, "end": v(-32, 83.5) * mm});
            skLineSegment(sketch, "E2.6.2.2", {"start": v(-17.5, 98) * mm, "end": v(-17.5, 83.5) * mm});
            skLineSegment(sketch, "E2.6.2.3", {"start": v(-17.5, 83.5) * mm, "end": v(-32, 83.5) * mm});
            skLineSegment(sketch, "E2.6.2.4", {"start": v(-17.5, 98) * mm, "end": v(-32, 98) * mm});
            skPoint(sketch, "E2.6.3.0", {"position": v(-24.75, 74.25) * mm});
            skLineSegment(sketch, "E2.6.3.1", {"start": v(-32, 81.5) * mm, "end": v(-32, 67) * mm});
            skLineSegment(sketch, "E2.6.3.2", {"start": v(-17.5, 81.5) * mm, "end": v(-17.5, 67) * mm});
            skLineSegment(sketch, "E2.6.3.3", {"start": v(-17.5, 67) * mm, "end": v(-32, 67) * mm});
            skLineSegment(sketch, "E2.6.3.4", {"start": v(-17.5, 81.5) * mm, "end": v(-32, 81.5) * mm});
            skPoint(sketch, "E2.6.4.0", {"position": v(-24.75, 57.75) * mm});
            skLineSegment(sketch, "E2.6.4.1", {"start": v(-32, 65) * mm, "end": v(-32, 50.5) * mm});
            skLineSegment(sketch, "E2.6.4.2", {"start": v(-17.5, 65) * mm, "end": v(-17.5, 50.5) * mm});
            skLineSegment(sketch, "E2.6.4.3", {"start": v(-17.5, 50.5) * mm, "end": v(-32, 50.5) * mm});
            skLineSegment(sketch, "E2.6.4.4", {"start": v(-17.5, 65) * mm, "end": v(-32, 65) * mm});
            skPoint(sketch, "E2.6.5.0", {"position": v(-24.75, 41.25) * mm});
            skLineSegment(sketch, "E2.6.5.1", {"start": v(-32, 48.5) * mm, "end": v(-32, 34) * mm});
            skLineSegment(sketch, "E2.6.5.2", {"start": v(-17.5, 48.5) * mm, "end": v(-17.5, 34) * mm});
            skLineSegment(sketch, "E2.6.5.3", {"start": v(-17.5, 34) * mm, "end": v(-32, 34) * mm});
            skLineSegment(sketch, "E2.6.5.4", {"start": v(-17.5, 48.5) * mm, "end": v(-32, 48.5) * mm});
            skPoint(sketch, "E2.6.6.0", {"position": v(-24.75, 24.75) * mm});
            skLineSegment(sketch, "E2.6.6.1", {"start": v(-32, 32) * mm, "end": v(-32, 17.5) * mm});
            skLineSegment(sketch, "E2.6.6.2", {"start": v(-17.5, 32) * mm, "end": v(-17.5, 17.5) * mm});
            skLineSegment(sketch, "E2.6.6.3", {"start": v(-17.5, 17.5) * mm, "end": v(-32, 17.5) * mm});
            skLineSegment(sketch, "E2.6.6.4", {"start": v(-17.5, 32) * mm, "end": v(-32, 32) * mm});
            skPoint(sketch, "E2.6.7.0", {"position": v(-24.75, 8.25) * mm});
            skLineSegment(sketch, "E2.6.7.1", {"start": v(-32, 15.5) * mm, "end": v(-32, 1) * mm});
            skLineSegment(sketch, "E2.6.7.2", {"start": v(-17.5, 15.5) * mm, "end": v(-17.5, 1) * mm});
            skLineSegment(sketch, "E2.6.7.3", {"start": v(-17.5, 1) * mm, "end": v(-32, 1) * mm});
            skLineSegment(sketch, "E2.6.7.4", {"start": v(-17.5, 15.5) * mm, "end": v(-32, 15.5) * mm});
            skPoint(sketch, "E2.6.8.0", {"position": v(-24.75, -8.25) * mm});
            skLineSegment(sketch, "E2.6.8.1", {"start": v(-32, -1) * mm, "end": v(-32, -15.5) * mm});
            skLineSegment(sketch, "E2.6.8.2", {"start": v(-17.5, -1) * mm, "end": v(-17.5, -15.5) * mm});
            skLineSegment(sketch, "E2.6.8.3", {"start": v(-17.5, -15.5) * mm, "end": v(-32, -15.5) * mm});
            skLineSegment(sketch, "E2.6.8.4", {"start": v(-17.5, -1) * mm, "end": v(-32, -1) * mm});
            skPoint(sketch, "E2.6.9.0", {"position": v(-24.75, -24.75) * mm});
            skLineSegment(sketch, "E2.6.9.1", {"start": v(-32, -17.5) * mm, "end": v(-32, -32) * mm});
            skLineSegment(sketch, "E2.6.9.2", {"start": v(-17.5, -17.5) * mm, "end": v(-17.5, -32) * mm});
            skLineSegment(sketch, "E2.6.9.3", {"start": v(-17.5, -32) * mm, "end": v(-32, -32) * mm});
            skLineSegment(sketch, "E2.6.9.4", {"start": v(-17.5, -17.5) * mm, "end": v(-32, -17.5) * mm});
            skPoint(sketch, "E2.6.10.0", {"position": v(-24.75, -41.25) * mm});
            skLineSegment(sketch, "E2.6.10.1", {"start": v(-32, -34) * mm, "end": v(-32, -48.5) * mm});
            skLineSegment(sketch, "E2.6.10.2", {"start": v(-17.5, -34) * mm, "end": v(-17.5, -48.5) * mm});
            skLineSegment(sketch, "E2.6.10.3", {"start": v(-17.5, -48.5) * mm, "end": v(-32, -48.5) * mm});
            skLineSegment(sketch, "E2.6.10.4", {"start": v(-17.5, -34) * mm, "end": v(-32, -34) * mm});
            skPoint(sketch, "E2.6.11.0", {"position": v(-24.75, -57.75) * mm});
            skLineSegment(sketch, "E2.6.11.1", {"start": v(-32, -50.5) * mm, "end": v(-32, -65) * mm});
            skLineSegment(sketch, "E2.6.11.2", {"start": v(-17.5, -50.5) * mm, "end": v(-17.5, -65) * mm});
            skLineSegment(sketch, "E2.6.11.3", {"start": v(-17.5, -65) * mm, "end": v(-32, -65) * mm});
            skLineSegment(sketch, "E2.6.11.4", {"start": v(-17.5, -50.5) * mm, "end": v(-32, -50.5) * mm});
            skPoint(sketch, "E2.6.12.0", {"position": v(-24.75, -74.25) * mm});
            skLineSegment(sketch, "E2.6.12.1", {"start": v(-32, -67) * mm, "end": v(-32, -81.5) * mm});
            skLineSegment(sketch, "E2.6.12.2", {"start": v(-17.5, -67) * mm, "end": v(-17.5, -81.5) * mm});
            skLineSegment(sketch, "E2.6.12.3", {"start": v(-17.5, -81.5) * mm, "end": v(-32, -81.5) * mm});
            skLineSegment(sketch, "E2.6.12.4", {"start": v(-17.5, -67) * mm, "end": v(-32, -67) * mm});
            skPoint(sketch, "E2.6.13.0", {"position": v(-24.75, -90.75) * mm});
            skLineSegment(sketch, "E2.6.13.1", {"start": v(-32, -83.5) * mm, "end": v(-32, -98) * mm});
            skLineSegment(sketch, "E2.6.13.2", {"start": v(-17.5, -83.5) * mm, "end": v(-17.5, -98) * mm});
            skLineSegment(sketch, "E2.6.13.3", {"start": v(-17.5, -98) * mm, "end": v(-32, -98) * mm});
            skLineSegment(sketch, "E2.6.13.4", {"start": v(-17.5, -83.5) * mm, "end": v(-32, -83.5) * mm});
            skPoint(sketch, "E2.6.14.0", {"position": v(-24.75, -107.25) * mm});
            skLineSegment(sketch, "E2.6.14.1", {"start": v(-32, -100) * mm, "end": v(-32, -114.5) * mm});
            skLineSegment(sketch, "E2.6.14.2", {"start": v(-17.5, -100) * mm, "end": v(-17.5, -114.5) * mm});
            skLineSegment(sketch, "E2.6.14.3", {"start": v(-17.5, -114.5) * mm, "end": v(-32, -114.5) * mm});
            skLineSegment(sketch, "E2.6.14.4", {"start": v(-17.5, -100) * mm, "end": v(-32, -100) * mm});
            skPoint(sketch, "E2.6.15.0", {"position": v(-24.75, -123.75) * mm});
            skLineSegment(sketch, "E2.6.15.1", {"start": v(-32, -116.5) * mm, "end": v(-32, -131) * mm});
            skLineSegment(sketch, "E2.6.15.2", {"start": v(-17.5, -116.5) * mm, "end": v(-17.5, -131) * mm});
            skLineSegment(sketch, "E2.6.15.3", {"start": v(-17.5, -131) * mm, "end": v(-32, -131) * mm});
            skLineSegment(sketch, "E2.6.15.4", {"start": v(-17.5, -116.5) * mm, "end": v(-32, -116.5) * mm});
            skPoint(sketch, "E2.7.0.0", {"position": v(-8.25, 123.75) * mm});
            skLineSegment(sketch, "E2.7.0.1", {"start": v(-15.5, 131) * mm, "end": v(-15.5, 116.5) * mm});
            skLineSegment(sketch, "E2.7.0.2", {"start": v(-1, 131) * mm, "end": v(-1, 116.5) * mm});
            skLineSegment(sketch, "E2.7.0.3", {"start": v(-1, 116.5) * mm, "end": v(-15.5, 116.5) * mm});
            skLineSegment(sketch, "E2.7.0.4", {"start": v(-1, 131) * mm, "end": v(-15.5, 131) * mm});
            skPoint(sketch, "E2.7.1.0", {"position": v(-8.25, 107.25) * mm});
            skLineSegment(sketch, "E2.7.1.1", {"start": v(-15.5, 114.5) * mm, "end": v(-15.5, 100) * mm});
            skLineSegment(sketch, "E2.7.1.2", {"start": v(-1, 114.5) * mm, "end": v(-1, 100) * mm});
            skLineSegment(sketch, "E2.7.1.3", {"start": v(-1, 100) * mm, "end": v(-15.5, 100) * mm});
            skLineSegment(sketch, "E2.7.1.4", {"start": v(-1, 114.5) * mm, "end": v(-15.5, 114.5) * mm});
            skPoint(sketch, "E2.7.2.0", {"position": v(-8.25, 90.75) * mm});
            skLineSegment(sketch, "E2.7.2.1", {"start": v(-15.5, 98) * mm, "end": v(-15.5, 83.5) * mm});
            skLineSegment(sketch, "E2.7.2.2", {"start": v(-1, 98) * mm, "end": v(-1, 83.5) * mm});
            skLineSegment(sketch, "E2.7.2.3", {"start": v(-1, 83.5) * mm, "end": v(-15.5, 83.5) * mm});
            skLineSegment(sketch, "E2.7.2.4", {"start": v(-1, 98) * mm, "end": v(-15.5, 98) * mm});
            skPoint(sketch, "E2.7.3.0", {"position": v(-8.25, 74.25) * mm});
            skLineSegment(sketch, "E2.7.3.1", {"start": v(-15.5, 81.5) * mm, "end": v(-15.5, 67) * mm});
            skLineSegment(sketch, "E2.7.3.2", {"start": v(-1, 81.5) * mm, "end": v(-1, 67) * mm});
            skLineSegment(sketch, "E2.7.3.3", {"start": v(-1, 67) * mm, "end": v(-15.5, 67) * mm});
            skLineSegment(sketch, "E2.7.3.4", {"start": v(-1, 81.5) * mm, "end": v(-15.5, 81.5) * mm});
            skPoint(sketch, "E2.7.4.0", {"position": v(-8.25, 57.75) * mm});
            skLineSegment(sketch, "E2.7.4.1", {"start": v(-15.5, 65) * mm, "end": v(-15.5, 50.5) * mm});
            skLineSegment(sketch, "E2.7.4.2", {"start": v(-1, 65) * mm, "end": v(-1, 50.5) * mm});
            skLineSegment(sketch, "E2.7.4.3", {"start": v(-1, 50.5) * mm, "end": v(-15.5, 50.5) * mm});
            skLineSegment(sketch, "E2.7.4.4", {"start": v(-1, 65) * mm, "end": v(-15.5, 65) * mm});
            skPoint(sketch, "E2.7.5.0", {"position": v(-8.25, 41.25) * mm});
            skLineSegment(sketch, "E2.7.5.1", {"start": v(-15.5, 48.5) * mm, "end": v(-15.5, 34) * mm});
            skLineSegment(sketch, "E2.7.5.2", {"start": v(-1, 48.5) * mm, "end": v(-1, 34) * mm});
            skLineSegment(sketch, "E2.7.5.3", {"start": v(-1, 34) * mm, "end": v(-15.5, 34) * mm});
            skLineSegment(sketch, "E2.7.5.4", {"start": v(-1, 48.5) * mm, "end": v(-15.5, 48.5) * mm});
            skPoint(sketch, "E2.7.6.0", {"position": v(-8.25, 24.75) * mm});
            skLineSegment(sketch, "E2.7.6.1", {"start": v(-15.5, 32) * mm, "end": v(-15.5, 17.5) * mm});
            skLineSegment(sketch, "E2.7.6.2", {"start": v(-1, 32) * mm, "end": v(-1, 17.5) * mm});
            skLineSegment(sketch, "E2.7.6.3", {"start": v(-1, 17.5) * mm, "end": v(-15.5, 17.5) * mm});
            skLineSegment(sketch, "E2.7.6.4", {"start": v(-1, 32) * mm, "end": v(-15.5, 32) * mm});
            skPoint(sketch, "E2.7.7.0", {"position": v(-8.25, 8.25) * mm});
            skLineSegment(sketch, "E2.7.7.1", {"start": v(-15.5, 15.5) * mm, "end": v(-15.5, 1) * mm});
            skLineSegment(sketch, "E2.7.7.2", {"start": v(-1, 15.5) * mm, "end": v(-1, 1) * mm});
            skLineSegment(sketch, "E2.7.7.3", {"start": v(-1, 1) * mm, "end": v(-15.5, 1) * mm});
            skLineSegment(sketch, "E2.7.7.4", {"start": v(-1, 15.5) * mm, "end": v(-15.5, 15.5) * mm});
            skPoint(sketch, "E2.7.8.0", {"position": v(-8.25, -8.25) * mm});
            skLineSegment(sketch, "E2.7.8.1", {"start": v(-15.5, -1) * mm, "end": v(-15.5, -15.5) * mm});
            skLineSegment(sketch, "E2.7.8.2", {"start": v(-1, -1) * mm, "end": v(-1, -15.5) * mm});
            skLineSegment(sketch, "E2.7.8.3", {"start": v(-1, -15.5) * mm, "end": v(-15.5, -15.5) * mm});
            skLineSegment(sketch, "E2.7.8.4", {"start": v(-1, -1) * mm, "end": v(-15.5, -1) * mm});
            skPoint(sketch, "E2.7.9.0", {"position": v(-8.25, -24.75) * mm});
            skLineSegment(sketch, "E2.7.9.1", {"start": v(-15.5, -17.5) * mm, "end": v(-15.5, -32) * mm});
            skLineSegment(sketch, "E2.7.9.2", {"start": v(-1, -17.5) * mm, "end": v(-1, -32) * mm});
            skLineSegment(sketch, "E2.7.9.3", {"start": v(-1, -32) * mm, "end": v(-15.5, -32) * mm});
            skLineSegment(sketch, "E2.7.9.4", {"start": v(-1, -17.5) * mm, "end": v(-15.5, -17.5) * mm});
            skPoint(sketch, "E2.7.10.0", {"position": v(-8.25, -41.25) * mm});
            skLineSegment(sketch, "E2.7.10.1", {"start": v(-15.5, -34) * mm, "end": v(-15.5, -48.5) * mm});
            skLineSegment(sketch, "E2.7.10.2", {"start": v(-1, -34) * mm, "end": v(-1, -48.5) * mm});
            skLineSegment(sketch, "E2.7.10.3", {"start": v(-1, -48.5) * mm, "end": v(-15.5, -48.5) * mm});
            skLineSegment(sketch, "E2.7.10.4", {"start": v(-1, -34) * mm, "end": v(-15.5, -34) * mm});
            skPoint(sketch, "E2.7.11.0", {"position": v(-8.25, -57.75) * mm});
            skLineSegment(sketch, "E2.7.11.1", {"start": v(-15.5, -50.5) * mm, "end": v(-15.5, -65) * mm});
            skLineSegment(sketch, "E2.7.11.2", {"start": v(-1, -50.5) * mm, "end": v(-1, -65) * mm});
            skLineSegment(sketch, "E2.7.11.3", {"start": v(-1, -65) * mm, "end": v(-15.5, -65) * mm});
            skLineSegment(sketch, "E2.7.11.4", {"start": v(-1, -50.5) * mm, "end": v(-15.5, -50.5) * mm});
            skPoint(sketch, "E2.7.12.0", {"position": v(-8.25, -74.25) * mm});
            skLineSegment(sketch, "E2.7.12.1", {"start": v(-15.5, -67) * mm, "end": v(-15.5, -81.5) * mm});
            skLineSegment(sketch, "E2.7.12.2", {"start": v(-1, -67) * mm, "end": v(-1, -81.5) * mm});
            skLineSegment(sketch, "E2.7.12.3", {"start": v(-1, -81.5) * mm, "end": v(-15.5, -81.5) * mm});
            skLineSegment(sketch, "E2.7.12.4", {"start": v(-1, -67) * mm, "end": v(-15.5, -67) * mm});
            skPoint(sketch, "E2.7.13.0", {"position": v(-8.25, -90.75) * mm});
            skLineSegment(sketch, "E2.7.13.1", {"start": v(-15.5, -83.5) * mm, "end": v(-15.5, -98) * mm});
            skLineSegment(sketch, "E2.7.13.2", {"start": v(-1, -83.5) * mm, "end": v(-1, -98) * mm});
            skLineSegment(sketch, "E2.7.13.3", {"start": v(-1, -98) * mm, "end": v(-15.5, -98) * mm});
            skLineSegment(sketch, "E2.7.13.4", {"start": v(-1, -83.5) * mm, "end": v(-15.5, -83.5) * mm});
            skPoint(sketch, "E2.7.14.0", {"position": v(-8.25, -107.25) * mm});
            skLineSegment(sketch, "E2.7.14.1", {"start": v(-15.5, -100) * mm, "end": v(-15.5, -114.5) * mm});
            skLineSegment(sketch, "E2.7.14.2", {"start": v(-1, -100) * mm, "end": v(-1, -114.5) * mm});
            skLineSegment(sketch, "E2.7.14.3", {"start": v(-1, -114.5) * mm, "end": v(-15.5, -114.5) * mm});
            skLineSegment(sketch, "E2.7.14.4", {"start": v(-1, -100) * mm, "end": v(-15.5, -100) * mm});
            skPoint(sketch, "E2.7.15.0", {"position": v(-8.25, -123.75) * mm});
            skLineSegment(sketch, "E2.7.15.1", {"start": v(-15.5, -116.5) * mm, "end": v(-15.5, -131) * mm});
            skLineSegment(sketch, "E2.7.15.2", {"start": v(-1, -116.5) * mm, "end": v(-1, -131) * mm});
            skLineSegment(sketch, "E2.7.15.3", {"start": v(-1, -131) * mm, "end": v(-15.5, -131) * mm});
            skLineSegment(sketch, "E2.7.15.4", {"start": v(-1, -116.5) * mm, "end": v(-15.5, -116.5) * mm});
            skPoint(sketch, "E2.8.0.0", {"position": v(8.25, 123.75) * mm});
            skLineSegment(sketch, "E2.8.0.1", {"start": v(1, 131) * mm, "end": v(1, 116.5) * mm});
            skLineSegment(sketch, "E2.8.0.2", {"start": v(15.5, 131) * mm, "end": v(15.5, 116.5) * mm});
            skLineSegment(sketch, "E2.8.0.3", {"start": v(15.5, 116.5) * mm, "end": v(1, 116.5) * mm});
            skLineSegment(sketch, "E2.8.0.4", {"start": v(15.5, 131) * mm, "end": v(1, 131) * mm});
            skPoint(sketch, "E2.8.1.0", {"position": v(8.25, 107.25) * mm});
            skLineSegment(sketch, "E2.8.1.1", {"start": v(1, 114.5) * mm, "end": v(1, 100) * mm});
            skLineSegment(sketch, "E2.8.1.2", {"start": v(15.5, 114.5) * mm, "end": v(15.5, 100) * mm});
            skLineSegment(sketch, "E2.8.1.3", {"start": v(15.5, 100) * mm, "end": v(1, 100) * mm});
            skLineSegment(sketch, "E2.8.1.4", {"start": v(15.5, 114.5) * mm, "end": v(1, 114.5) * mm});
            skPoint(sketch, "E2.8.2.0", {"position": v(8.25, 90.75) * mm});
            skLineSegment(sketch, "E2.8.2.1", {"start": v(1, 98) * mm, "end": v(1, 83.5) * mm});
            skLineSegment(sketch, "E2.8.2.2", {"start": v(15.5, 98) * mm, "end": v(15.5, 83.5) * mm});
            skLineSegment(sketch, "E2.8.2.3", {"start": v(15.5, 83.5) * mm, "end": v(1, 83.5) * mm});
            skLineSegment(sketch, "E2.8.2.4", {"start": v(15.5, 98) * mm, "end": v(1, 98) * mm});
            skPoint(sketch, "E2.8.3.0", {"position": v(8.25, 74.25) * mm});
            skLineSegment(sketch, "E2.8.3.1", {"start": v(1, 81.5) * mm, "end": v(1, 67) * mm});
            skLineSegment(sketch, "E2.8.3.2", {"start": v(15.5, 81.5) * mm, "end": v(15.5, 67) * mm});
            skLineSegment(sketch, "E2.8.3.3", {"start": v(15.5, 67) * mm, "end": v(1, 67) * mm});
            skLineSegment(sketch, "E2.8.3.4", {"start": v(15.5, 81.5) * mm, "end": v(1, 81.5) * mm});
            skPoint(sketch, "E2.8.4.0", {"position": v(8.25, 57.75) * mm});
            skLineSegment(sketch, "E2.8.4.1", {"start": v(1, 65) * mm, "end": v(1, 50.5) * mm});
            skLineSegment(sketch, "E2.8.4.2", {"start": v(15.5, 65) * mm, "end": v(15.5, 50.5) * mm});
            skLineSegment(sketch, "E2.8.4.3", {"start": v(15.5, 50.5) * mm, "end": v(1, 50.5) * mm});
            skLineSegment(sketch, "E2.8.4.4", {"start": v(15.5, 65) * mm, "end": v(1, 65) * mm});
            skPoint(sketch, "E2.8.5.0", {"position": v(8.25, 41.25) * mm});
            skLineSegment(sketch, "E2.8.5.1", {"start": v(1, 48.5) * mm, "end": v(1, 34) * mm});
            skLineSegment(sketch, "E2.8.5.2", {"start": v(15.5, 48.5) * mm, "end": v(15.5, 34) * mm});
            skLineSegment(sketch, "E2.8.5.3", {"start": v(15.5, 34) * mm, "end": v(1, 34) * mm});
            skLineSegment(sketch, "E2.8.5.4", {"start": v(15.5, 48.5) * mm, "end": v(1, 48.5) * mm});
            skPoint(sketch, "E2.8.6.0", {"position": v(8.25, 24.75) * mm});
            skLineSegment(sketch, "E2.8.6.1", {"start": v(1, 32) * mm, "end": v(1, 17.5) * mm});
            skLineSegment(sketch, "E2.8.6.2", {"start": v(15.5, 32) * mm, "end": v(15.5, 17.5) * mm});
            skLineSegment(sketch, "E2.8.6.3", {"start": v(15.5, 17.5) * mm, "end": v(1, 17.5) * mm});
            skLineSegment(sketch, "E2.8.6.4", {"start": v(15.5, 32) * mm, "end": v(1, 32) * mm});
            skPoint(sketch, "E2.8.7.0", {"position": v(8.25, 8.25) * mm});
            skLineSegment(sketch, "E2.8.7.1", {"start": v(1, 15.5) * mm, "end": v(1, 1) * mm});
            skLineSegment(sketch, "E2.8.7.2", {"start": v(15.5, 15.5) * mm, "end": v(15.5, 1) * mm});
            skLineSegment(sketch, "E2.8.7.3", {"start": v(15.5, 1) * mm, "end": v(1, 1) * mm});
            skLineSegment(sketch, "E2.8.7.4", {"start": v(15.5, 15.5) * mm, "end": v(1, 15.5) * mm});
            skPoint(sketch, "E2.8.8.0", {"position": v(8.25, -8.25) * mm});
            skLineSegment(sketch, "E2.8.8.1", {"start": v(1, -1) * mm, "end": v(1, -15.5) * mm});
            skLineSegment(sketch, "E2.8.8.2", {"start": v(15.5, -1) * mm, "end": v(15.5, -15.5) * mm});
            skLineSegment(sketch, "E2.8.8.3", {"start": v(15.5, -15.5) * mm, "end": v(1, -15.5) * mm});
            skLineSegment(sketch, "E2.8.8.4", {"start": v(15.5, -1) * mm, "end": v(1, -1) * mm});
            skPoint(sketch, "E2.8.9.0", {"position": v(8.25, -24.75) * mm});
            skLineSegment(sketch, "E2.8.9.1", {"start": v(1, -17.5) * mm, "end": v(1, -32) * mm});
            skLineSegment(sketch, "E2.8.9.2", {"start": v(15.5, -17.5) * mm, "end": v(15.5, -32) * mm});
            skLineSegment(sketch, "E2.8.9.3", {"start": v(15.5, -32) * mm, "end": v(1, -32) * mm});
            skLineSegment(sketch, "E2.8.9.4", {"start": v(15.5, -17.5) * mm, "end": v(1, -17.5) * mm});
            skPoint(sketch, "E2.8.10.0", {"position": v(8.25, -41.25) * mm});
            skLineSegment(sketch, "E2.8.10.1", {"start": v(1, -34) * mm, "end": v(1, -48.5) * mm});
            skLineSegment(sketch, "E2.8.10.2", {"start": v(15.5, -34) * mm, "end": v(15.5, -48.5) * mm});
            skLineSegment(sketch, "E2.8.10.3", {"start": v(15.5, -48.5) * mm, "end": v(1, -48.5) * mm});
            skLineSegment(sketch, "E2.8.10.4", {"start": v(15.5, -34) * mm, "end": v(1, -34) * mm});
            skPoint(sketch, "E2.8.11.0", {"position": v(8.25, -57.75) * mm});
            skLineSegment(sketch, "E2.8.11.1", {"start": v(1, -50.5) * mm, "end": v(1, -65) * mm});
            skLineSegment(sketch, "E2.8.11.2", {"start": v(15.5, -50.5) * mm, "end": v(15.5, -65) * mm});
            skLineSegment(sketch, "E2.8.11.3", {"start": v(15.5, -65) * mm, "end": v(1, -65) * mm});
            skLineSegment(sketch, "E2.8.11.4", {"start": v(15.5, -50.5) * mm, "end": v(1, -50.5) * mm});
            skPoint(sketch, "E2.8.12.0", {"position": v(8.25, -74.25) * mm});
            skLineSegment(sketch, "E2.8.12.1", {"start": v(1, -67) * mm, "end": v(1, -81.5) * mm});
            skLineSegment(sketch, "E2.8.12.2", {"start": v(15.5, -67) * mm, "end": v(15.5, -81.5) * mm});
            skLineSegment(sketch, "E2.8.12.3", {"start": v(15.5, -81.5) * mm, "end": v(1, -81.5) * mm});
            skLineSegment(sketch, "E2.8.12.4", {"start": v(15.5, -67) * mm, "end": v(1, -67) * mm});
            skPoint(sketch, "E2.8.13.0", {"position": v(8.25, -90.75) * mm});
            skLineSegment(sketch, "E2.8.13.1", {"start": v(1, -83.5) * mm, "end": v(1, -98) * mm});
            skLineSegment(sketch, "E2.8.13.2", {"start": v(15.5, -83.5) * mm, "end": v(15.5, -98) * mm});
            skLineSegment(sketch, "E2.8.13.3", {"start": v(15.5, -98) * mm, "end": v(1, -98) * mm});
            skLineSegment(sketch, "E2.8.13.4", {"start": v(15.5, -83.5) * mm, "end": v(1, -83.5) * mm});
            skPoint(sketch, "E2.8.14.0", {"position": v(8.25, -107.25) * mm});
            skLineSegment(sketch, "E2.8.14.1", {"start": v(1, -100) * mm, "end": v(1, -114.5) * mm});
            skLineSegment(sketch, "E2.8.14.2", {"start": v(15.5, -100) * mm, "end": v(15.5, -114.5) * mm});
            skLineSegment(sketch, "E2.8.14.3", {"start": v(15.5, -114.5) * mm, "end": v(1, -114.5) * mm});
            skLineSegment(sketch, "E2.8.14.4", {"start": v(15.5, -100) * mm, "end": v(1, -100) * mm});
            skPoint(sketch, "E2.8.15.0", {"position": v(8.25, -123.75) * mm});
            skLineSegment(sketch, "E2.8.15.1", {"start": v(1, -116.5) * mm, "end": v(1, -131) * mm});
            skLineSegment(sketch, "E2.8.15.2", {"start": v(15.5, -116.5) * mm, "end": v(15.5, -131) * mm});
            skLineSegment(sketch, "E2.8.15.3", {"start": v(15.5, -131) * mm, "end": v(1, -131) * mm});
            skLineSegment(sketch, "E2.8.15.4", {"start": v(15.5, -116.5) * mm, "end": v(1, -116.5) * mm});
            skPoint(sketch, "E2.9.0.0", {"position": v(24.75, 123.75) * mm});
            skLineSegment(sketch, "E2.9.0.1", {"start": v(17.5, 131) * mm, "end": v(17.5, 116.5) * mm});
            skLineSegment(sketch, "E2.9.0.2", {"start": v(32, 131) * mm, "end": v(32, 116.5) * mm});
            skLineSegment(sketch, "E2.9.0.3", {"start": v(32, 116.5) * mm, "end": v(17.5, 116.5) * mm});
            skLineSegment(sketch, "E2.9.0.4", {"start": v(32, 131) * mm, "end": v(17.5, 131) * mm});
            skPoint(sketch, "E2.9.1.0", {"position": v(24.75, 107.25) * mm});
            skLineSegment(sketch, "E2.9.1.1", {"start": v(17.5, 114.5) * mm, "end": v(17.5, 100) * mm});
            skLineSegment(sketch, "E2.9.1.2", {"start": v(32, 114.5) * mm, "end": v(32, 100) * mm});
            skLineSegment(sketch, "E2.9.1.3", {"start": v(32, 100) * mm, "end": v(17.5, 100) * mm});
            skLineSegment(sketch, "E2.9.1.4", {"start": v(32, 114.5) * mm, "end": v(17.5, 114.5) * mm});
            skPoint(sketch, "E2.9.2.0", {"position": v(24.75, 90.75) * mm});
            skLineSegment(sketch, "E2.9.2.1", {"start": v(17.5, 98) * mm, "end": v(17.5, 83.5) * mm});
            skLineSegment(sketch, "E2.9.2.2", {"start": v(32, 98) * mm, "end": v(32, 83.5) * mm});
            skLineSegment(sketch, "E2.9.2.3", {"start": v(32, 83.5) * mm, "end": v(17.5, 83.5) * mm});
            skLineSegment(sketch, "E2.9.2.4", {"start": v(32, 98) * mm, "end": v(17.5, 98) * mm});
            skPoint(sketch, "E2.9.3.0", {"position": v(24.75, 74.25) * mm});
            skLineSegment(sketch, "E2.9.3.1", {"start": v(17.5, 81.5) * mm, "end": v(17.5, 67) * mm});
            skLineSegment(sketch, "E2.9.3.2", {"start": v(32, 81.5) * mm, "end": v(32, 67) * mm});
            skLineSegment(sketch, "E2.9.3.3", {"start": v(32, 67) * mm, "end": v(17.5, 67) * mm});
            skLineSegment(sketch, "E2.9.3.4", {"start": v(32, 81.5) * mm, "end": v(17.5, 81.5) * mm});
            skPoint(sketch, "E2.9.4.0", {"position": v(24.75, 57.75) * mm});
            skLineSegment(sketch, "E2.9.4.1", {"start": v(17.5, 65) * mm, "end": v(17.5, 50.5) * mm});
            skLineSegment(sketch, "E2.9.4.2", {"start": v(32, 65) * mm, "end": v(32, 50.5) * mm});
            skLineSegment(sketch, "E2.9.4.3", {"start": v(32, 50.5) * mm, "end": v(17.5, 50.5) * mm});
            skLineSegment(sketch, "E2.9.4.4", {"start": v(32, 65) * mm, "end": v(17.5, 65) * mm});
            skPoint(sketch, "E2.9.5.0", {"position": v(24.75, 41.25) * mm});
            skLineSegment(sketch, "E2.9.5.1", {"start": v(17.5, 48.5) * mm, "end": v(17.5, 34) * mm});
            skLineSegment(sketch, "E2.9.5.2", {"start": v(32, 48.5) * mm, "end": v(32, 34) * mm});
            skLineSegment(sketch, "E2.9.5.3", {"start": v(32, 34) * mm, "end": v(17.5, 34) * mm});
            skLineSegment(sketch, "E2.9.5.4", {"start": v(32, 48.5) * mm, "end": v(17.5, 48.5) * mm});
            skPoint(sketch, "E2.9.6.0", {"position": v(24.75, 24.75) * mm});
            skLineSegment(sketch, "E2.9.6.1", {"start": v(17.5, 32) * mm, "end": v(17.5, 17.5) * mm});
            skLineSegment(sketch, "E2.9.6.2", {"start": v(32, 32) * mm, "end": v(32, 17.5) * mm});
            skLineSegment(sketch, "E2.9.6.3", {"start": v(32, 17.5) * mm, "end": v(17.5, 17.5) * mm});
            skLineSegment(sketch, "E2.9.6.4", {"start": v(32, 32) * mm, "end": v(17.5, 32) * mm});
            skPoint(sketch, "E2.9.7.0", {"position": v(24.75, 8.25) * mm});
            skLineSegment(sketch, "E2.9.7.1", {"start": v(17.5, 15.5) * mm, "end": v(17.5, 1) * mm});
            skLineSegment(sketch, "E2.9.7.2", {"start": v(32, 15.5) * mm, "end": v(32, 1) * mm});
            skLineSegment(sketch, "E2.9.7.3", {"start": v(32, 1) * mm, "end": v(17.5, 1) * mm});
            skLineSegment(sketch, "E2.9.7.4", {"start": v(32, 15.5) * mm, "end": v(17.5, 15.5) * mm});
            skPoint(sketch, "E2.9.8.0", {"position": v(24.75, -8.25) * mm});
            skLineSegment(sketch, "E2.9.8.1", {"start": v(17.5, -1) * mm, "end": v(17.5, -15.5) * mm});
            skLineSegment(sketch, "E2.9.8.2", {"start": v(32, -1) * mm, "end": v(32, -15.5) * mm});
            skLineSegment(sketch, "E2.9.8.3", {"start": v(32, -15.5) * mm, "end": v(17.5, -15.5) * mm});
            skLineSegment(sketch, "E2.9.8.4", {"start": v(32, -1) * mm, "end": v(17.5, -1) * mm});
            skPoint(sketch, "E2.9.9.0", {"position": v(24.75, -24.75) * mm});
            skLineSegment(sketch, "E2.9.9.1", {"start": v(17.5, -17.5) * mm, "end": v(17.5, -32) * mm});
            skLineSegment(sketch, "E2.9.9.2", {"start": v(32, -17.5) * mm, "end": v(32, -32) * mm});
            skLineSegment(sketch, "E2.9.9.3", {"start": v(32, -32) * mm, "end": v(17.5, -32) * mm});
            skLineSegment(sketch, "E2.9.9.4", {"start": v(32, -17.5) * mm, "end": v(17.5, -17.5) * mm});
            skPoint(sketch, "E2.9.10.0", {"position": v(24.75, -41.25) * mm});
            skLineSegment(sketch, "E2.9.10.1", {"start": v(17.5, -34) * mm, "end": v(17.5, -48.5) * mm});
            skLineSegment(sketch, "E2.9.10.2", {"start": v(32, -34) * mm, "end": v(32, -48.5) * mm});
            skLineSegment(sketch, "E2.9.10.3", {"start": v(32, -48.5) * mm, "end": v(17.5, -48.5) * mm});
            skLineSegment(sketch, "E2.9.10.4", {"start": v(32, -34) * mm, "end": v(17.5, -34) * mm});
            skPoint(sketch, "E2.9.11.0", {"position": v(24.75, -57.75) * mm});
            skLineSegment(sketch, "E2.9.11.1", {"start": v(17.5, -50.5) * mm, "end": v(17.5, -65) * mm});
            skLineSegment(sketch, "E2.9.11.2", {"start": v(32, -50.5) * mm, "end": v(32, -65) * mm});
            skLineSegment(sketch, "E2.9.11.3", {"start": v(32, -65) * mm, "end": v(17.5, -65) * mm});
            skLineSegment(sketch, "E2.9.11.4", {"start": v(32, -50.5) * mm, "end": v(17.5, -50.5) * mm});
            skPoint(sketch, "E2.9.12.0", {"position": v(24.75, -74.25) * mm});
            skLineSegment(sketch, "E2.9.12.1", {"start": v(17.5, -67) * mm, "end": v(17.5, -81.5) * mm});
            skLineSegment(sketch, "E2.9.12.2", {"start": v(32, -67) * mm, "end": v(32, -81.5) * mm});
            skLineSegment(sketch, "E2.9.12.3", {"start": v(32, -81.5) * mm, "end": v(17.5, -81.5) * mm});
            skLineSegment(sketch, "E2.9.12.4", {"start": v(32, -67) * mm, "end": v(17.5, -67) * mm});
            skPoint(sketch, "E2.9.13.0", {"position": v(24.75, -90.75) * mm});
            skLineSegment(sketch, "E2.9.13.1", {"start": v(17.5, -83.5) * mm, "end": v(17.5, -98) * mm});
            skLineSegment(sketch, "E2.9.13.2", {"start": v(32, -83.5) * mm, "end": v(32, -98) * mm});
            skLineSegment(sketch, "E2.9.13.3", {"start": v(32, -98) * mm, "end": v(17.5, -98) * mm});
            skLineSegment(sketch, "E2.9.13.4", {"start": v(32, -83.5) * mm, "end": v(17.5, -83.5) * mm});
            skPoint(sketch, "E2.9.14.0", {"position": v(24.75, -107.25) * mm});
            skLineSegment(sketch, "E2.9.14.1", {"start": v(17.5, -100) * mm, "end": v(17.5, -114.5) * mm});
            skLineSegment(sketch, "E2.9.14.2", {"start": v(32, -100) * mm, "end": v(32, -114.5) * mm});
            skLineSegment(sketch, "E2.9.14.3", {"start": v(32, -114.5) * mm, "end": v(17.5, -114.5) * mm});
            skLineSegment(sketch, "E2.9.14.4", {"start": v(32, -100) * mm, "end": v(17.5, -100) * mm});
            skPoint(sketch, "E2.9.15.0", {"position": v(24.75, -123.75) * mm});
            skLineSegment(sketch, "E2.9.15.1", {"start": v(17.5, -116.5) * mm, "end": v(17.5, -131) * mm});
            skLineSegment(sketch, "E2.9.15.2", {"start": v(32, -116.5) * mm, "end": v(32, -131) * mm});
            skLineSegment(sketch, "E2.9.15.3", {"start": v(32, -131) * mm, "end": v(17.5, -131) * mm});
            skLineSegment(sketch, "E2.9.15.4", {"start": v(32, -116.5) * mm, "end": v(17.5, -116.5) * mm});
            skPoint(sketch, "E2.10.0.0", {"position": v(41.25, 123.75) * mm});
            skLineSegment(sketch, "E2.10.0.1", {"start": v(34, 131) * mm, "end": v(34, 116.5) * mm});
            skLineSegment(sketch, "E2.10.0.2", {"start": v(48.5, 131) * mm, "end": v(48.5, 116.5) * mm});
            skLineSegment(sketch, "E2.10.0.3", {"start": v(48.5, 116.5) * mm, "end": v(34, 116.5) * mm});
            skLineSegment(sketch, "E2.10.0.4", {"start": v(48.5, 131) * mm, "end": v(34, 131) * mm});
            skPoint(sketch, "E2.10.1.0", {"position": v(41.25, 107.25) * mm});
            skLineSegment(sketch, "E2.10.1.1", {"start": v(34, 114.5) * mm, "end": v(34, 100) * mm});
            skLineSegment(sketch, "E2.10.1.2", {"start": v(48.5, 114.5) * mm, "end": v(48.5, 100) * mm});
            skLineSegment(sketch, "E2.10.1.3", {"start": v(48.5, 100) * mm, "end": v(34, 100) * mm});
            skLineSegment(sketch, "E2.10.1.4", {"start": v(48.5, 114.5) * mm, "end": v(34, 114.5) * mm});
            skPoint(sketch, "E2.10.2.0", {"position": v(41.25, 90.75) * mm});
            skLineSegment(sketch, "E2.10.2.1", {"start": v(34, 98) * mm, "end": v(34, 83.5) * mm});
            skLineSegment(sketch, "E2.10.2.2", {"start": v(48.5, 98) * mm, "end": v(48.5, 83.5) * mm});
            skLineSegment(sketch, "E2.10.2.3", {"start": v(48.5, 83.5) * mm, "end": v(34, 83.5) * mm});
            skLineSegment(sketch, "E2.10.2.4", {"start": v(48.5, 98) * mm, "end": v(34, 98) * mm});
            skPoint(sketch, "E2.10.3.0", {"position": v(41.25, 74.25) * mm});
            skLineSegment(sketch, "E2.10.3.1", {"start": v(34, 81.5) * mm, "end": v(34, 67) * mm});
            skLineSegment(sketch, "E2.10.3.2", {"start": v(48.5, 81.5) * mm, "end": v(48.5, 67) * mm});
            skLineSegment(sketch, "E2.10.3.3", {"start": v(48.5, 67) * mm, "end": v(34, 67) * mm});
            skLineSegment(sketch, "E2.10.3.4", {"start": v(48.5, 81.5) * mm, "end": v(34, 81.5) * mm});
            skPoint(sketch, "E2.10.4.0", {"position": v(41.25, 57.75) * mm});
            skLineSegment(sketch, "E2.10.4.1", {"start": v(34, 65) * mm, "end": v(34, 50.5) * mm});
            skLineSegment(sketch, "E2.10.4.2", {"start": v(48.5, 65) * mm, "end": v(48.5, 50.5) * mm});
            skLineSegment(sketch, "E2.10.4.3", {"start": v(48.5, 50.5) * mm, "end": v(34, 50.5) * mm});
            skLineSegment(sketch, "E2.10.4.4", {"start": v(48.5, 65) * mm, "end": v(34, 65) * mm});
            skPoint(sketch, "E2.10.5.0", {"position": v(41.25, 41.25) * mm});
            skLineSegment(sketch, "E2.10.5.1", {"start": v(34, 48.5) * mm, "end": v(34, 34) * mm});
            skLineSegment(sketch, "E2.10.5.2", {"start": v(48.5, 48.5) * mm, "end": v(48.5, 34) * mm});
            skLineSegment(sketch, "E2.10.5.3", {"start": v(48.5, 34) * mm, "end": v(34, 34) * mm});
            skLineSegment(sketch, "E2.10.5.4", {"start": v(48.5, 48.5) * mm, "end": v(34, 48.5) * mm});
            skPoint(sketch, "E2.10.6.0", {"position": v(41.25, 24.75) * mm});
            skLineSegment(sketch, "E2.10.6.1", {"start": v(34, 32) * mm, "end": v(34, 17.5) * mm});
            skLineSegment(sketch, "E2.10.6.2", {"start": v(48.5, 32) * mm, "end": v(48.5, 17.5) * mm});
            skLineSegment(sketch, "E2.10.6.3", {"start": v(48.5, 17.5) * mm, "end": v(34, 17.5) * mm});
            skLineSegment(sketch, "E2.10.6.4", {"start": v(48.5, 32) * mm, "end": v(34, 32) * mm});
            skPoint(sketch, "E2.10.7.0", {"position": v(41.25, 8.25) * mm});
            skLineSegment(sketch, "E2.10.7.1", {"start": v(34, 15.5) * mm, "end": v(34, 1) * mm});
            skLineSegment(sketch, "E2.10.7.2", {"start": v(48.5, 15.5) * mm, "end": v(48.5, 1) * mm});
            skLineSegment(sketch, "E2.10.7.3", {"start": v(48.5, 1) * mm, "end": v(34, 1) * mm});
            skLineSegment(sketch, "E2.10.7.4", {"start": v(48.5, 15.5) * mm, "end": v(34, 15.5) * mm});
            skPoint(sketch, "E2.10.8.0", {"position": v(41.25, -8.25) * mm});
            skLineSegment(sketch, "E2.10.8.1", {"start": v(34, -1) * mm, "end": v(34, -15.5) * mm});
            skLineSegment(sketch, "E2.10.8.2", {"start": v(48.5, -1) * mm, "end": v(48.5, -15.5) * mm});
            skLineSegment(sketch, "E2.10.8.3", {"start": v(48.5, -15.5) * mm, "end": v(34, -15.5) * mm});
            skLineSegment(sketch, "E2.10.8.4", {"start": v(48.5, -1) * mm, "end": v(34, -1) * mm});
            skPoint(sketch, "E2.10.9.0", {"position": v(41.25, -24.75) * mm});
            skLineSegment(sketch, "E2.10.9.1", {"start": v(34, -17.5) * mm, "end": v(34, -32) * mm});
            skLineSegment(sketch, "E2.10.9.2", {"start": v(48.5, -17.5) * mm, "end": v(48.5, -32) * mm});
            skLineSegment(sketch, "E2.10.9.3", {"start": v(48.5, -32) * mm, "end": v(34, -32) * mm});
            skLineSegment(sketch, "E2.10.9.4", {"start": v(48.5, -17.5) * mm, "end": v(34, -17.5) * mm});
            skPoint(sketch, "E2.10.10.0", {"position": v(41.25, -41.25) * mm});
            skLineSegment(sketch, "E2.10.10.1", {"start": v(34, -34) * mm, "end": v(34, -48.5) * mm});
            skLineSegment(sketch, "E2.10.10.2", {"start": v(48.5, -34) * mm, "end": v(48.5, -48.5) * mm});
            skLineSegment(sketch, "E2.10.10.3", {"start": v(48.5, -48.5) * mm, "end": v(34, -48.5) * mm});
            skLineSegment(sketch, "E2.10.10.4", {"start": v(48.5, -34) * mm, "end": v(34, -34) * mm});
            skPoint(sketch, "E2.10.11.0", {"position": v(41.25, -57.75) * mm});
            skLineSegment(sketch, "E2.10.11.1", {"start": v(34, -50.5) * mm, "end": v(34, -65) * mm});
            skLineSegment(sketch, "E2.10.11.2", {"start": v(48.5, -50.5) * mm, "end": v(48.5, -65) * mm});
            skLineSegment(sketch, "E2.10.11.3", {"start": v(48.5, -65) * mm, "end": v(34, -65) * mm});
            skLineSegment(sketch, "E2.10.11.4", {"start": v(48.5, -50.5) * mm, "end": v(34, -50.5) * mm});
            skPoint(sketch, "E2.10.12.0", {"position": v(41.25, -74.25) * mm});
            skLineSegment(sketch, "E2.10.12.1", {"start": v(34, -67) * mm, "end": v(34, -81.5) * mm});
            skLineSegment(sketch, "E2.10.12.2", {"start": v(48.5, -67) * mm, "end": v(48.5, -81.5) * mm});
            skLineSegment(sketch, "E2.10.12.3", {"start": v(48.5, -81.5) * mm, "end": v(34, -81.5) * mm});
            skLineSegment(sketch, "E2.10.12.4", {"start": v(48.5, -67) * mm, "end": v(34, -67) * mm});
            skPoint(sketch, "E2.10.13.0", {"position": v(41.25, -90.75) * mm});
            skLineSegment(sketch, "E2.10.13.1", {"start": v(34, -83.5) * mm, "end": v(34, -98) * mm});
            skLineSegment(sketch, "E2.10.13.2", {"start": v(48.5, -83.5) * mm, "end": v(48.5, -98) * mm});
            skLineSegment(sketch, "E2.10.13.3", {"start": v(48.5, -98) * mm, "end": v(34, -98) * mm});
            skLineSegment(sketch, "E2.10.13.4", {"start": v(48.5, -83.5) * mm, "end": v(34, -83.5) * mm});
            skPoint(sketch, "E2.10.14.0", {"position": v(41.25, -107.25) * mm});
            skLineSegment(sketch, "E2.10.14.1", {"start": v(34, -100) * mm, "end": v(34, -114.5) * mm});
            skLineSegment(sketch, "E2.10.14.2", {"start": v(48.5, -100) * mm, "end": v(48.5, -114.5) * mm});
            skLineSegment(sketch, "E2.10.14.3", {"start": v(48.5, -114.5) * mm, "end": v(34, -114.5) * mm});
            skLineSegment(sketch, "E2.10.14.4", {"start": v(48.5, -100) * mm, "end": v(34, -100) * mm});
            skPoint(sketch, "E2.10.15.0", {"position": v(41.25, -123.75) * mm});
            skLineSegment(sketch, "E2.10.15.1", {"start": v(34, -116.5) * mm, "end": v(34, -131) * mm});
            skLineSegment(sketch, "E2.10.15.2", {"start": v(48.5, -116.5) * mm, "end": v(48.5, -131) * mm});
            skLineSegment(sketch, "E2.10.15.3", {"start": v(48.5, -131) * mm, "end": v(34, -131) * mm});
            skLineSegment(sketch, "E2.10.15.4", {"start": v(48.5, -116.5) * mm, "end": v(34, -116.5) * mm});
            skPoint(sketch, "E2.11.0.0", {"position": v(57.75, 123.75) * mm});
            skLineSegment(sketch, "E2.11.0.1", {"start": v(50.5, 131) * mm, "end": v(50.5, 116.5) * mm});
            skLineSegment(sketch, "E2.11.0.2", {"start": v(65, 131) * mm, "end": v(65, 116.5) * mm});
            skLineSegment(sketch, "E2.11.0.3", {"start": v(65, 116.5) * mm, "end": v(50.5, 116.5) * mm});
            skLineSegment(sketch, "E2.11.0.4", {"start": v(65, 131) * mm, "end": v(50.5, 131) * mm});
            skPoint(sketch, "E2.11.1.0", {"position": v(57.75, 107.25) * mm});
            skLineSegment(sketch, "E2.11.1.1", {"start": v(50.5, 114.5) * mm, "end": v(50.5, 100) * mm});
            skLineSegment(sketch, "E2.11.1.2", {"start": v(65, 114.5) * mm, "end": v(65, 100) * mm});
            skLineSegment(sketch, "E2.11.1.3", {"start": v(65, 100) * mm, "end": v(50.5, 100) * mm});
            skLineSegment(sketch, "E2.11.1.4", {"start": v(65, 114.5) * mm, "end": v(50.5, 114.5) * mm});
            skPoint(sketch, "E2.11.2.0", {"position": v(57.75, 90.75) * mm});
            skLineSegment(sketch, "E2.11.2.1", {"start": v(50.5, 98) * mm, "end": v(50.5, 83.5) * mm});
            skLineSegment(sketch, "E2.11.2.2", {"start": v(65, 98) * mm, "end": v(65, 83.5) * mm});
            skLineSegment(sketch, "E2.11.2.3", {"start": v(65, 83.5) * mm, "end": v(50.5, 83.5) * mm});
            skLineSegment(sketch, "E2.11.2.4", {"start": v(65, 98) * mm, "end": v(50.5, 98) * mm});
            skPoint(sketch, "E2.11.3.0", {"position": v(57.75, 74.25) * mm});
            skLineSegment(sketch, "E2.11.3.1", {"start": v(50.5, 81.5) * mm, "end": v(50.5, 67) * mm});
            skLineSegment(sketch, "E2.11.3.2", {"start": v(65, 81.5) * mm, "end": v(65, 67) * mm});
            skLineSegment(sketch, "E2.11.3.3", {"start": v(65, 67) * mm, "end": v(50.5, 67) * mm});
            skLineSegment(sketch, "E2.11.3.4", {"start": v(65, 81.5) * mm, "end": v(50.5, 81.5) * mm});
            skPoint(sketch, "E2.11.4.0", {"position": v(57.75, 57.75) * mm});
            skLineSegment(sketch, "E2.11.4.1", {"start": v(50.5, 65) * mm, "end": v(50.5, 50.5) * mm});
            skLineSegment(sketch, "E2.11.4.2", {"start": v(65, 65) * mm, "end": v(65, 50.5) * mm});
            skLineSegment(sketch, "E2.11.4.3", {"start": v(65, 50.5) * mm, "end": v(50.5, 50.5) * mm});
            skLineSegment(sketch, "E2.11.4.4", {"start": v(65, 65) * mm, "end": v(50.5, 65) * mm});
            skPoint(sketch, "E2.11.5.0", {"position": v(57.75, 41.25) * mm});
            skLineSegment(sketch, "E2.11.5.1", {"start": v(50.5, 48.5) * mm, "end": v(50.5, 34) * mm});
            skLineSegment(sketch, "E2.11.5.2", {"start": v(65, 48.5) * mm, "end": v(65, 34) * mm});
            skLineSegment(sketch, "E2.11.5.3", {"start": v(65, 34) * mm, "end": v(50.5, 34) * mm});
            skLineSegment(sketch, "E2.11.5.4", {"start": v(65, 48.5) * mm, "end": v(50.5, 48.5) * mm});
            skPoint(sketch, "E2.11.6.0", {"position": v(57.75, 24.75) * mm});
            skLineSegment(sketch, "E2.11.6.1", {"start": v(50.5, 32) * mm, "end": v(50.5, 17.5) * mm});
            skLineSegment(sketch, "E2.11.6.2", {"start": v(65, 32) * mm, "end": v(65, 17.5) * mm});
            skLineSegment(sketch, "E2.11.6.3", {"start": v(65, 17.5) * mm, "end": v(50.5, 17.5) * mm});
            skLineSegment(sketch, "E2.11.6.4", {"start": v(65, 32) * mm, "end": v(50.5, 32) * mm});
            skPoint(sketch, "E2.11.7.0", {"position": v(57.75, 8.25) * mm});
            skLineSegment(sketch, "E2.11.7.1", {"start": v(50.5, 15.5) * mm, "end": v(50.5, 1) * mm});
            skLineSegment(sketch, "E2.11.7.2", {"start": v(65, 15.5) * mm, "end": v(65, 1) * mm});
            skLineSegment(sketch, "E2.11.7.3", {"start": v(65, 1) * mm, "end": v(50.5, 1) * mm});
            skLineSegment(sketch, "E2.11.7.4", {"start": v(65, 15.5) * mm, "end": v(50.5, 15.5) * mm});
            skPoint(sketch, "E2.11.8.0", {"position": v(57.75, -8.25) * mm});
            skLineSegment(sketch, "E2.11.8.1", {"start": v(50.5, -1) * mm, "end": v(50.5, -15.5) * mm});
            skLineSegment(sketch, "E2.11.8.2", {"start": v(65, -1) * mm, "end": v(65, -15.5) * mm});
            skLineSegment(sketch, "E2.11.8.3", {"start": v(65, -15.5) * mm, "end": v(50.5, -15.5) * mm});
            skLineSegment(sketch, "E2.11.8.4", {"start": v(65, -1) * mm, "end": v(50.5, -1) * mm});
            skPoint(sketch, "E2.11.9.0", {"position": v(57.75, -24.75) * mm});
            skLineSegment(sketch, "E2.11.9.1", {"start": v(50.5, -17.5) * mm, "end": v(50.5, -32) * mm});
            skLineSegment(sketch, "E2.11.9.2", {"start": v(65, -17.5) * mm, "end": v(65, -32) * mm});
            skLineSegment(sketch, "E2.11.9.3", {"start": v(65, -32) * mm, "end": v(50.5, -32) * mm});
            skLineSegment(sketch, "E2.11.9.4", {"start": v(65, -17.5) * mm, "end": v(50.5, -17.5) * mm});
            skPoint(sketch, "E2.11.10.0", {"position": v(57.75, -41.25) * mm});
            skLineSegment(sketch, "E2.11.10.1", {"start": v(50.5, -34) * mm, "end": v(50.5, -48.5) * mm});
            skLineSegment(sketch, "E2.11.10.2", {"start": v(65, -34) * mm, "end": v(65, -48.5) * mm});
            skLineSegment(sketch, "E2.11.10.3", {"start": v(65, -48.5) * mm, "end": v(50.5, -48.5) * mm});
            skLineSegment(sketch, "E2.11.10.4", {"start": v(65, -34) * mm, "end": v(50.5, -34) * mm});
            skPoint(sketch, "E2.11.11.0", {"position": v(57.75, -57.75) * mm});
            skLineSegment(sketch, "E2.11.11.1", {"start": v(50.5, -50.5) * mm, "end": v(50.5, -65) * mm});
            skLineSegment(sketch, "E2.11.11.2", {"start": v(65, -50.5) * mm, "end": v(65, -65) * mm});
            skLineSegment(sketch, "E2.11.11.3", {"start": v(65, -65) * mm, "end": v(50.5, -65) * mm});
            skLineSegment(sketch, "E2.11.11.4", {"start": v(65, -50.5) * mm, "end": v(50.5, -50.5) * mm});
            skPoint(sketch, "E2.11.12.0", {"position": v(57.75, -74.25) * mm});
            skLineSegment(sketch, "E2.11.12.1", {"start": v(50.5, -67) * mm, "end": v(50.5, -81.5) * mm});
            skLineSegment(sketch, "E2.11.12.2", {"start": v(65, -67) * mm, "end": v(65, -81.5) * mm});
            skLineSegment(sketch, "E2.11.12.3", {"start": v(65, -81.5) * mm, "end": v(50.5, -81.5) * mm});
            skLineSegment(sketch, "E2.11.12.4", {"start": v(65, -67) * mm, "end": v(50.5, -67) * mm});
            skPoint(sketch, "E2.11.13.0", {"position": v(57.75, -90.75) * mm});
            skLineSegment(sketch, "E2.11.13.1", {"start": v(50.5, -83.5) * mm, "end": v(50.5, -98) * mm});
            skLineSegment(sketch, "E2.11.13.2", {"start": v(65, -83.5) * mm, "end": v(65, -98) * mm});
            skLineSegment(sketch, "E2.11.13.3", {"start": v(65, -98) * mm, "end": v(50.5, -98) * mm});
            skLineSegment(sketch, "E2.11.13.4", {"start": v(65, -83.5) * mm, "end": v(50.5, -83.5) * mm});
            skPoint(sketch, "E2.11.14.0", {"position": v(57.75, -107.25) * mm});
            skLineSegment(sketch, "E2.11.14.1", {"start": v(50.5, -100) * mm, "end": v(50.5, -114.5) * mm});
            skLineSegment(sketch, "E2.11.14.2", {"start": v(65, -100) * mm, "end": v(65, -114.5) * mm});
            skLineSegment(sketch, "E2.11.14.3", {"start": v(65, -114.5) * mm, "end": v(50.5, -114.5) * mm});
            skLineSegment(sketch, "E2.11.14.4", {"start": v(65, -100) * mm, "end": v(50.5, -100) * mm});
            skPoint(sketch, "E2.11.15.0", {"position": v(57.75, -123.75) * mm});
            skLineSegment(sketch, "E2.11.15.1", {"start": v(50.5, -116.5) * mm, "end": v(50.5, -131) * mm});
            skLineSegment(sketch, "E2.11.15.2", {"start": v(65, -116.5) * mm, "end": v(65, -131) * mm});
            skLineSegment(sketch, "E2.11.15.3", {"start": v(65, -131) * mm, "end": v(50.5, -131) * mm});
            skLineSegment(sketch, "E2.11.15.4", {"start": v(65, -116.5) * mm, "end": v(50.5, -116.5) * mm});
            skPoint(sketch, "E2.12.0.0", {"position": v(74.25, 123.75) * mm});
            skLineSegment(sketch, "E2.12.0.1", {"start": v(67, 131) * mm, "end": v(67, 116.5) * mm});
            skLineSegment(sketch, "E2.12.0.2", {"start": v(81.5, 131) * mm, "end": v(81.5, 116.5) * mm});
            skLineSegment(sketch, "E2.12.0.3", {"start": v(81.5, 116.5) * mm, "end": v(67, 116.5) * mm});
            skLineSegment(sketch, "E2.12.0.4", {"start": v(81.5, 131) * mm, "end": v(67, 131) * mm});
            skPoint(sketch, "E2.12.1.0", {"position": v(74.25, 107.25) * mm});
            skLineSegment(sketch, "E2.12.1.1", {"start": v(67, 114.5) * mm, "end": v(67, 100) * mm});
            skLineSegment(sketch, "E2.12.1.2", {"start": v(81.5, 114.5) * mm, "end": v(81.5, 100) * mm});
            skLineSegment(sketch, "E2.12.1.3", {"start": v(81.5, 100) * mm, "end": v(67, 100) * mm});
            skLineSegment(sketch, "E2.12.1.4", {"start": v(81.5, 114.5) * mm, "end": v(67, 114.5) * mm});
            skPoint(sketch, "E2.12.2.0", {"position": v(74.25, 90.75) * mm});
            skLineSegment(sketch, "E2.12.2.1", {"start": v(67, 98) * mm, "end": v(67, 83.5) * mm});
            skLineSegment(sketch, "E2.12.2.2", {"start": v(81.5, 98) * mm, "end": v(81.5, 83.5) * mm});
            skLineSegment(sketch, "E2.12.2.3", {"start": v(81.5, 83.5) * mm, "end": v(67, 83.5) * mm});
            skLineSegment(sketch, "E2.12.2.4", {"start": v(81.5, 98) * mm, "end": v(67, 98) * mm});
            skPoint(sketch, "E2.12.3.0", {"position": v(74.25, 74.25) * mm});
            skLineSegment(sketch, "E2.12.3.1", {"start": v(67, 81.5) * mm, "end": v(67, 67) * mm});
            skLineSegment(sketch, "E2.12.3.2", {"start": v(81.5, 81.5) * mm, "end": v(81.5, 67) * mm});
            skLineSegment(sketch, "E2.12.3.3", {"start": v(81.5, 67) * mm, "end": v(67, 67) * mm});
            skLineSegment(sketch, "E2.12.3.4", {"start": v(81.5, 81.5) * mm, "end": v(67, 81.5) * mm});
            skPoint(sketch, "E2.12.4.0", {"position": v(74.25, 57.75) * mm});
            skLineSegment(sketch, "E2.12.4.1", {"start": v(67, 65) * mm, "end": v(67, 50.5) * mm});
            skLineSegment(sketch, "E2.12.4.2", {"start": v(81.5, 65) * mm, "end": v(81.5, 50.5) * mm});
            skLineSegment(sketch, "E2.12.4.3", {"start": v(81.5, 50.5) * mm, "end": v(67, 50.5) * mm});
            skLineSegment(sketch, "E2.12.4.4", {"start": v(81.5, 65) * mm, "end": v(67, 65) * mm});
            skPoint(sketch, "E2.12.5.0", {"position": v(74.25, 41.25) * mm});
            skLineSegment(sketch, "E2.12.5.1", {"start": v(67, 48.5) * mm, "end": v(67, 34) * mm});
            skLineSegment(sketch, "E2.12.5.2", {"start": v(81.5, 48.5) * mm, "end": v(81.5, 34) * mm});
            skLineSegment(sketch, "E2.12.5.3", {"start": v(81.5, 34) * mm, "end": v(67, 34) * mm});
            skLineSegment(sketch, "E2.12.5.4", {"start": v(81.5, 48.5) * mm, "end": v(67, 48.5) * mm});
            skPoint(sketch, "E2.12.6.0", {"position": v(74.25, 24.75) * mm});
            skLineSegment(sketch, "E2.12.6.1", {"start": v(67, 32) * mm, "end": v(67, 17.5) * mm});
            skLineSegment(sketch, "E2.12.6.2", {"start": v(81.5, 32) * mm, "end": v(81.5, 17.5) * mm});
            skLineSegment(sketch, "E2.12.6.3", {"start": v(81.5, 17.5) * mm, "end": v(67, 17.5) * mm});
            skLineSegment(sketch, "E2.12.6.4", {"start": v(81.5, 32) * mm, "end": v(67, 32) * mm});
            skPoint(sketch, "E2.12.7.0", {"position": v(74.25, 8.25) * mm});
            skLineSegment(sketch, "E2.12.7.1", {"start": v(67, 15.5) * mm, "end": v(67, 1) * mm});
            skLineSegment(sketch, "E2.12.7.2", {"start": v(81.5, 15.5) * mm, "end": v(81.5, 1) * mm});
            skLineSegment(sketch, "E2.12.7.3", {"start": v(81.5, 1) * mm, "end": v(67, 1) * mm});
            skLineSegment(sketch, "E2.12.7.4", {"start": v(81.5, 15.5) * mm, "end": v(67, 15.5) * mm});
            skPoint(sketch, "E2.12.8.0", {"position": v(74.25, -8.25) * mm});
            skLineSegment(sketch, "E2.12.8.1", {"start": v(67, -1) * mm, "end": v(67, -15.5) * mm});
            skLineSegment(sketch, "E2.12.8.2", {"start": v(81.5, -1) * mm, "end": v(81.5, -15.5) * mm});
            skLineSegment(sketch, "E2.12.8.3", {"start": v(81.5, -15.5) * mm, "end": v(67, -15.5) * mm});
            skLineSegment(sketch, "E2.12.8.4", {"start": v(81.5, -1) * mm, "end": v(67, -1) * mm});
            skPoint(sketch, "E2.12.9.0", {"position": v(74.25, -24.75) * mm});
            skLineSegment(sketch, "E2.12.9.1", {"start": v(67, -17.5) * mm, "end": v(67, -32) * mm});
            skLineSegment(sketch, "E2.12.9.2", {"start": v(81.5, -17.5) * mm, "end": v(81.5, -32) * mm});
            skLineSegment(sketch, "E2.12.9.3", {"start": v(81.5, -32) * mm, "end": v(67, -32) * mm});
            skLineSegment(sketch, "E2.12.9.4", {"start": v(81.5, -17.5) * mm, "end": v(67, -17.5) * mm});
            skPoint(sketch, "E2.12.10.0", {"position": v(74.25, -41.25) * mm});
            skLineSegment(sketch, "E2.12.10.1", {"start": v(67, -34) * mm, "end": v(67, -48.5) * mm});
            skLineSegment(sketch, "E2.12.10.2", {"start": v(81.5, -34) * mm, "end": v(81.5, -48.5) * mm});
            skLineSegment(sketch, "E2.12.10.3", {"start": v(81.5, -48.5) * mm, "end": v(67, -48.5) * mm});
            skLineSegment(sketch, "E2.12.10.4", {"start": v(81.5, -34) * mm, "end": v(67, -34) * mm});
            skPoint(sketch, "E2.12.11.0", {"position": v(74.25, -57.75) * mm});
            skLineSegment(sketch, "E2.12.11.1", {"start": v(67, -50.5) * mm, "end": v(67, -65) * mm});
            skLineSegment(sketch, "E2.12.11.2", {"start": v(81.5, -50.5) * mm, "end": v(81.5, -65) * mm});
            skLineSegment(sketch, "E2.12.11.3", {"start": v(81.5, -65) * mm, "end": v(67, -65) * mm});
            skLineSegment(sketch, "E2.12.11.4", {"start": v(81.5, -50.5) * mm, "end": v(67, -50.5) * mm});
            skPoint(sketch, "E2.12.12.0", {"position": v(74.25, -74.25) * mm});
            skLineSegment(sketch, "E2.12.12.1", {"start": v(67, -67) * mm, "end": v(67, -81.5) * mm});
            skLineSegment(sketch, "E2.12.12.2", {"start": v(81.5, -67) * mm, "end": v(81.5, -81.5) * mm});
            skLineSegment(sketch, "E2.12.12.3", {"start": v(81.5, -81.5) * mm, "end": v(67, -81.5) * mm});
            skLineSegment(sketch, "E2.12.12.4", {"start": v(81.5, -67) * mm, "end": v(67, -67) * mm});
            skPoint(sketch, "E2.12.13.0", {"position": v(74.25, -90.75) * mm});
            skLineSegment(sketch, "E2.12.13.1", {"start": v(67, -83.5) * mm, "end": v(67, -98) * mm});
            skLineSegment(sketch, "E2.12.13.2", {"start": v(81.5, -83.5) * mm, "end": v(81.5, -98) * mm});
            skLineSegment(sketch, "E2.12.13.3", {"start": v(81.5, -98) * mm, "end": v(67, -98) * mm});
            skLineSegment(sketch, "E2.12.13.4", {"start": v(81.5, -83.5) * mm, "end": v(67, -83.5) * mm});
            skPoint(sketch, "E2.12.14.0", {"position": v(74.25, -107.25) * mm});
            skLineSegment(sketch, "E2.12.14.1", {"start": v(67, -100) * mm, "end": v(67, -114.5) * mm});
            skLineSegment(sketch, "E2.12.14.2", {"start": v(81.5, -100) * mm, "end": v(81.5, -114.5) * mm});
            skLineSegment(sketch, "E2.12.14.3", {"start": v(81.5, -114.5) * mm, "end": v(67, -114.5) * mm});
            skLineSegment(sketch, "E2.12.14.4", {"start": v(81.5, -100) * mm, "end": v(67, -100) * mm});
            skPoint(sketch, "E2.12.15.0", {"position": v(74.25, -123.75) * mm});
            skLineSegment(sketch, "E2.12.15.1", {"start": v(67, -116.5) * mm, "end": v(67, -131) * mm});
            skLineSegment(sketch, "E2.12.15.2", {"start": v(81.5, -116.5) * mm, "end": v(81.5, -131) * mm});
            skLineSegment(sketch, "E2.12.15.3", {"start": v(81.5, -131) * mm, "end": v(67, -131) * mm});
            skLineSegment(sketch, "E2.12.15.4", {"start": v(81.5, -116.5) * mm, "end": v(67, -116.5) * mm});
            skPoint(sketch, "E2.13.0.0", {"position": v(90.75, 123.75) * mm});
            skLineSegment(sketch, "E2.13.0.1", {"start": v(83.5, 131) * mm, "end": v(83.5, 116.5) * mm});
            skLineSegment(sketch, "E2.13.0.2", {"start": v(98, 131) * mm, "end": v(98, 116.5) * mm});
            skLineSegment(sketch, "E2.13.0.3", {"start": v(98, 116.5) * mm, "end": v(83.5, 116.5) * mm});
            skLineSegment(sketch, "E2.13.0.4", {"start": v(98, 131) * mm, "end": v(83.5, 131) * mm});
            skPoint(sketch, "E2.13.1.0", {"position": v(90.75, 107.25) * mm});
            skLineSegment(sketch, "E2.13.1.1", {"start": v(83.5, 114.5) * mm, "end": v(83.5, 100) * mm});
            skLineSegment(sketch, "E2.13.1.2", {"start": v(98, 114.5) * mm, "end": v(98, 100) * mm});
            skLineSegment(sketch, "E2.13.1.3", {"start": v(98, 100) * mm, "end": v(83.5, 100) * mm});
            skLineSegment(sketch, "E2.13.1.4", {"start": v(98, 114.5) * mm, "end": v(83.5, 114.5) * mm});
            skPoint(sketch, "E2.13.2.0", {"position": v(90.75, 90.75) * mm});
            skLineSegment(sketch, "E2.13.2.1", {"start": v(83.5, 98) * mm, "end": v(83.5, 83.5) * mm});
            skLineSegment(sketch, "E2.13.2.2", {"start": v(98, 98) * mm, "end": v(98, 83.5) * mm});
            skLineSegment(sketch, "E2.13.2.3", {"start": v(98, 83.5) * mm, "end": v(83.5, 83.5) * mm});
            skLineSegment(sketch, "E2.13.2.4", {"start": v(98, 98) * mm, "end": v(83.5, 98) * mm});
            skPoint(sketch, "E2.13.3.0", {"position": v(90.75, 74.25) * mm});
            skLineSegment(sketch, "E2.13.3.1", {"start": v(83.5, 81.5) * mm, "end": v(83.5, 67) * mm});
            skLineSegment(sketch, "E2.13.3.2", {"start": v(98, 81.5) * mm, "end": v(98, 67) * mm});
            skLineSegment(sketch, "E2.13.3.3", {"start": v(98, 67) * mm, "end": v(83.5, 67) * mm});
            skLineSegment(sketch, "E2.13.3.4", {"start": v(98, 81.5) * mm, "end": v(83.5, 81.5) * mm});
            skPoint(sketch, "E2.13.4.0", {"position": v(90.75, 57.75) * mm});
            skLineSegment(sketch, "E2.13.4.1", {"start": v(83.5, 65) * mm, "end": v(83.5, 50.5) * mm});
            skLineSegment(sketch, "E2.13.4.2", {"start": v(98, 65) * mm, "end": v(98, 50.5) * mm});
            skLineSegment(sketch, "E2.13.4.3", {"start": v(98, 50.5) * mm, "end": v(83.5, 50.5) * mm});
            skLineSegment(sketch, "E2.13.4.4", {"start": v(98, 65) * mm, "end": v(83.5, 65) * mm});
            skPoint(sketch, "E2.13.5.0", {"position": v(90.75, 41.25) * mm});
            skLineSegment(sketch, "E2.13.5.1", {"start": v(83.5, 48.5) * mm, "end": v(83.5, 34) * mm});
            skLineSegment(sketch, "E2.13.5.2", {"start": v(98, 48.5) * mm, "end": v(98, 34) * mm});
            skLineSegment(sketch, "E2.13.5.3", {"start": v(98, 34) * mm, "end": v(83.5, 34) * mm});
            skLineSegment(sketch, "E2.13.5.4", {"start": v(98, 48.5) * mm, "end": v(83.5, 48.5) * mm});
            skPoint(sketch, "E2.13.6.0", {"position": v(90.75, 24.75) * mm});
            skLineSegment(sketch, "E2.13.6.1", {"start": v(83.5, 32) * mm, "end": v(83.5, 17.5) * mm});
            skLineSegment(sketch, "E2.13.6.2", {"start": v(98, 32) * mm, "end": v(98, 17.5) * mm});
            skLineSegment(sketch, "E2.13.6.3", {"start": v(98, 17.5) * mm, "end": v(83.5, 17.5) * mm});
            skLineSegment(sketch, "E2.13.6.4", {"start": v(98, 32) * mm, "end": v(83.5, 32) * mm});
            skPoint(sketch, "E2.13.7.0", {"position": v(90.75, 8.25) * mm});
            skLineSegment(sketch, "E2.13.7.1", {"start": v(83.5, 15.5) * mm, "end": v(83.5, 1) * mm});
            skLineSegment(sketch, "E2.13.7.2", {"start": v(98, 15.5) * mm, "end": v(98, 1) * mm});
            skLineSegment(sketch, "E2.13.7.3", {"start": v(98, 1) * mm, "end": v(83.5, 1) * mm});
            skLineSegment(sketch, "E2.13.7.4", {"start": v(98, 15.5) * mm, "end": v(83.5, 15.5) * mm});
            skPoint(sketch, "E2.13.8.0", {"position": v(90.75, -8.25) * mm});
            skLineSegment(sketch, "E2.13.8.1", {"start": v(83.5, -1) * mm, "end": v(83.5, -15.5) * mm});
            skLineSegment(sketch, "E2.13.8.2", {"start": v(98, -1) * mm, "end": v(98, -15.5) * mm});
            skLineSegment(sketch, "E2.13.8.3", {"start": v(98, -15.5) * mm, "end": v(83.5, -15.5) * mm});
            skLineSegment(sketch, "E2.13.8.4", {"start": v(98, -1) * mm, "end": v(83.5, -1) * mm});
            skPoint(sketch, "E2.13.9.0", {"position": v(90.75, -24.75) * mm});
            skLineSegment(sketch, "E2.13.9.1", {"start": v(83.5, -17.5) * mm, "end": v(83.5, -32) * mm});
            skLineSegment(sketch, "E2.13.9.2", {"start": v(98, -17.5) * mm, "end": v(98, -32) * mm});
            skLineSegment(sketch, "E2.13.9.3", {"start": v(98, -32) * mm, "end": v(83.5, -32) * mm});
            skLineSegment(sketch, "E2.13.9.4", {"start": v(98, -17.5) * mm, "end": v(83.5, -17.5) * mm});
            skPoint(sketch, "E2.13.10.0", {"position": v(90.75, -41.25) * mm});
            skLineSegment(sketch, "E2.13.10.1", {"start": v(83.5, -34) * mm, "end": v(83.5, -48.5) * mm});
            skLineSegment(sketch, "E2.13.10.2", {"start": v(98, -34) * mm, "end": v(98, -48.5) * mm});
            skLineSegment(sketch, "E2.13.10.3", {"start": v(98, -48.5) * mm, "end": v(83.5, -48.5) * mm});
            skLineSegment(sketch, "E2.13.10.4", {"start": v(98, -34) * mm, "end": v(83.5, -34) * mm});
            skPoint(sketch, "E2.13.11.0", {"position": v(90.75, -57.75) * mm});
            skLineSegment(sketch, "E2.13.11.1", {"start": v(83.5, -50.5) * mm, "end": v(83.5, -65) * mm});
            skLineSegment(sketch, "E2.13.11.2", {"start": v(98, -50.5) * mm, "end": v(98, -65) * mm});
            skLineSegment(sketch, "E2.13.11.3", {"start": v(98, -65) * mm, "end": v(83.5, -65) * mm});
            skLineSegment(sketch, "E2.13.11.4", {"start": v(98, -50.5) * mm, "end": v(83.5, -50.5) * mm});
            skPoint(sketch, "E2.13.12.0", {"position": v(90.75, -74.25) * mm});
            skLineSegment(sketch, "E2.13.12.1", {"start": v(83.5, -67) * mm, "end": v(83.5, -81.5) * mm});
            skLineSegment(sketch, "E2.13.12.2", {"start": v(98, -67) * mm, "end": v(98, -81.5) * mm});
            skLineSegment(sketch, "E2.13.12.3", {"start": v(98, -81.5) * mm, "end": v(83.5, -81.5) * mm});
            skLineSegment(sketch, "E2.13.12.4", {"start": v(98, -67) * mm, "end": v(83.5, -67) * mm});
            skPoint(sketch, "E2.13.13.0", {"position": v(90.75, -90.75) * mm});
            skLineSegment(sketch, "E2.13.13.1", {"start": v(83.5, -83.5) * mm, "end": v(83.5, -98) * mm});
            skLineSegment(sketch, "E2.13.13.2", {"start": v(98, -83.5) * mm, "end": v(98, -98) * mm});
            skLineSegment(sketch, "E2.13.13.3", {"start": v(98, -98) * mm, "end": v(83.5, -98) * mm});
            skLineSegment(sketch, "E2.13.13.4", {"start": v(98, -83.5) * mm, "end": v(83.5, -83.5) * mm});
            skPoint(sketch, "E2.13.14.0", {"position": v(90.75, -107.25) * mm});
            skLineSegment(sketch, "E2.13.14.1", {"start": v(83.5, -100) * mm, "end": v(83.5, -114.5) * mm});
            skLineSegment(sketch, "E2.13.14.2", {"start": v(98, -100) * mm, "end": v(98, -114.5) * mm});
            skLineSegment(sketch, "E2.13.14.3", {"start": v(98, -114.5) * mm, "end": v(83.5, -114.5) * mm});
            skLineSegment(sketch, "E2.13.14.4", {"start": v(98, -100) * mm, "end": v(83.5, -100) * mm});
            skPoint(sketch, "E2.13.15.0", {"position": v(90.75, -123.75) * mm});
            skLineSegment(sketch, "E2.13.15.1", {"start": v(83.5, -116.5) * mm, "end": v(83.5, -131) * mm});
            skLineSegment(sketch, "E2.13.15.2", {"start": v(98, -116.5) * mm, "end": v(98, -131) * mm});
            skLineSegment(sketch, "E2.13.15.3", {"start": v(98, -131) * mm, "end": v(83.5, -131) * mm});
            skLineSegment(sketch, "E2.13.15.4", {"start": v(98, -116.5) * mm, "end": v(83.5, -116.5) * mm});
            skPoint(sketch, "E2.14.0.0", {"position": v(107.25, 123.75) * mm});
            skLineSegment(sketch, "E2.14.0.1", {"start": v(100, 131) * mm, "end": v(100, 116.5) * mm});
            skLineSegment(sketch, "E2.14.0.2", {"start": v(114.5, 131) * mm, "end": v(114.5, 116.5) * mm});
            skLineSegment(sketch, "E2.14.0.3", {"start": v(114.5, 116.5) * mm, "end": v(100, 116.5) * mm});
            skLineSegment(sketch, "E2.14.0.4", {"start": v(114.5, 131) * mm, "end": v(100, 131) * mm});
            skPoint(sketch, "E2.14.1.0", {"position": v(107.25, 107.25) * mm});
            skLineSegment(sketch, "E2.14.1.1", {"start": v(100, 114.5) * mm, "end": v(100, 100) * mm});
            skLineSegment(sketch, "E2.14.1.2", {"start": v(114.5, 114.5) * mm, "end": v(114.5, 100) * mm});
            skLineSegment(sketch, "E2.14.1.3", {"start": v(114.5, 100) * mm, "end": v(100, 100) * mm});
            skLineSegment(sketch, "E2.14.1.4", {"start": v(114.5, 114.5) * mm, "end": v(100, 114.5) * mm});
            skPoint(sketch, "E2.14.2.0", {"position": v(107.25, 90.75) * mm});
            skLineSegment(sketch, "E2.14.2.1", {"start": v(100, 98) * mm, "end": v(100, 83.5) * mm});
            skLineSegment(sketch, "E2.14.2.2", {"start": v(114.5, 98) * mm, "end": v(114.5, 83.5) * mm});
            skLineSegment(sketch, "E2.14.2.3", {"start": v(114.5, 83.5) * mm, "end": v(100, 83.5) * mm});
            skLineSegment(sketch, "E2.14.2.4", {"start": v(114.5, 98) * mm, "end": v(100, 98) * mm});
            skPoint(sketch, "E2.14.3.0", {"position": v(107.25, 74.25) * mm});
            skLineSegment(sketch, "E2.14.3.1", {"start": v(100, 81.5) * mm, "end": v(100, 67) * mm});
            skLineSegment(sketch, "E2.14.3.2", {"start": v(114.5, 81.5) * mm, "end": v(114.5, 67) * mm});
            skLineSegment(sketch, "E2.14.3.3", {"start": v(114.5, 67) * mm, "end": v(100, 67) * mm});
            skLineSegment(sketch, "E2.14.3.4", {"start": v(114.5, 81.5) * mm, "end": v(100, 81.5) * mm});
            skPoint(sketch, "E2.14.4.0", {"position": v(107.25, 57.75) * mm});
            skLineSegment(sketch, "E2.14.4.1", {"start": v(100, 65) * mm, "end": v(100, 50.5) * mm});
            skLineSegment(sketch, "E2.14.4.2", {"start": v(114.5, 65) * mm, "end": v(114.5, 50.5) * mm});
            skLineSegment(sketch, "E2.14.4.3", {"start": v(114.5, 50.5) * mm, "end": v(100, 50.5) * mm});
            skLineSegment(sketch, "E2.14.4.4", {"start": v(114.5, 65) * mm, "end": v(100, 65) * mm});
            skPoint(sketch, "E2.14.5.0", {"position": v(107.25, 41.25) * mm});
            skLineSegment(sketch, "E2.14.5.1", {"start": v(100, 48.5) * mm, "end": v(100, 34) * mm});
            skLineSegment(sketch, "E2.14.5.2", {"start": v(114.5, 48.5) * mm, "end": v(114.5, 34) * mm});
            skLineSegment(sketch, "E2.14.5.3", {"start": v(114.5, 34) * mm, "end": v(100, 34) * mm});
            skLineSegment(sketch, "E2.14.5.4", {"start": v(114.5, 48.5) * mm, "end": v(100, 48.5) * mm});
            skPoint(sketch, "E2.14.6.0", {"position": v(107.25, 24.75) * mm});
            skLineSegment(sketch, "E2.14.6.1", {"start": v(100, 32) * mm, "end": v(100, 17.5) * mm});
            skLineSegment(sketch, "E2.14.6.2", {"start": v(114.5, 32) * mm, "end": v(114.5, 17.5) * mm});
            skLineSegment(sketch, "E2.14.6.3", {"start": v(114.5, 17.5) * mm, "end": v(100, 17.5) * mm});
            skLineSegment(sketch, "E2.14.6.4", {"start": v(114.5, 32) * mm, "end": v(100, 32) * mm});
            skPoint(sketch, "E2.14.7.0", {"position": v(107.25, 8.25) * mm});
            skLineSegment(sketch, "E2.14.7.1", {"start": v(100, 15.5) * mm, "end": v(100, 1) * mm});
            skLineSegment(sketch, "E2.14.7.2", {"start": v(114.5, 15.5) * mm, "end": v(114.5, 1) * mm});
            skLineSegment(sketch, "E2.14.7.3", {"start": v(114.5, 1) * mm, "end": v(100, 1) * mm});
            skLineSegment(sketch, "E2.14.7.4", {"start": v(114.5, 15.5) * mm, "end": v(100, 15.5) * mm});
            skPoint(sketch, "E2.14.8.0", {"position": v(107.25, -8.25) * mm});
            skLineSegment(sketch, "E2.14.8.1", {"start": v(100, -1) * mm, "end": v(100, -15.5) * mm});
            skLineSegment(sketch, "E2.14.8.2", {"start": v(114.5, -1) * mm, "end": v(114.5, -15.5) * mm});
            skLineSegment(sketch, "E2.14.8.3", {"start": v(114.5, -15.5) * mm, "end": v(100, -15.5) * mm});
            skLineSegment(sketch, "E2.14.8.4", {"start": v(114.5, -1) * mm, "end": v(100, -1) * mm});
            skPoint(sketch, "E2.14.9.0", {"position": v(107.25, -24.75) * mm});
            skLineSegment(sketch, "E2.14.9.1", {"start": v(100, -17.5) * mm, "end": v(100, -32) * mm});
            skLineSegment(sketch, "E2.14.9.2", {"start": v(114.5, -17.5) * mm, "end": v(114.5, -32) * mm});
            skLineSegment(sketch, "E2.14.9.3", {"start": v(114.5, -32) * mm, "end": v(100, -32) * mm});
            skLineSegment(sketch, "E2.14.9.4", {"start": v(114.5, -17.5) * mm, "end": v(100, -17.5) * mm});
            skPoint(sketch, "E2.14.10.0", {"position": v(107.25, -41.25) * mm});
            skLineSegment(sketch, "E2.14.10.1", {"start": v(100, -34) * mm, "end": v(100, -48.5) * mm});
            skLineSegment(sketch, "E2.14.10.2", {"start": v(114.5, -34) * mm, "end": v(114.5, -48.5) * mm});
            skLineSegment(sketch, "E2.14.10.3", {"start": v(114.5, -48.5) * mm, "end": v(100, -48.5) * mm});
            skLineSegment(sketch, "E2.14.10.4", {"start": v(114.5, -34) * mm, "end": v(100, -34) * mm});
            skPoint(sketch, "E2.14.11.0", {"position": v(107.25, -57.75) * mm});
            skLineSegment(sketch, "E2.14.11.1", {"start": v(100, -50.5) * mm, "end": v(100, -65) * mm});
            skLineSegment(sketch, "E2.14.11.2", {"start": v(114.5, -50.5) * mm, "end": v(114.5, -65) * mm});
            skLineSegment(sketch, "E2.14.11.3", {"start": v(114.5, -65) * mm, "end": v(100, -65) * mm});
            skLineSegment(sketch, "E2.14.11.4", {"start": v(114.5, -50.5) * mm, "end": v(100, -50.5) * mm});
            skPoint(sketch, "E2.14.12.0", {"position": v(107.25, -74.25) * mm});
            skLineSegment(sketch, "E2.14.12.1", {"start": v(100, -67) * mm, "end": v(100, -81.5) * mm});
            skLineSegment(sketch, "E2.14.12.2", {"start": v(114.5, -67) * mm, "end": v(114.5, -81.5) * mm});
            skLineSegment(sketch, "E2.14.12.3", {"start": v(114.5, -81.5) * mm, "end": v(100, -81.5) * mm});
            skLineSegment(sketch, "E2.14.12.4", {"start": v(114.5, -67) * mm, "end": v(100, -67) * mm});
            skPoint(sketch, "E2.14.13.0", {"position": v(107.25, -90.75) * mm});
            skLineSegment(sketch, "E2.14.13.1", {"start": v(100, -83.5) * mm, "end": v(100, -98) * mm});
            skLineSegment(sketch, "E2.14.13.2", {"start": v(114.5, -83.5) * mm, "end": v(114.5, -98) * mm});
            skLineSegment(sketch, "E2.14.13.3", {"start": v(114.5, -98) * mm, "end": v(100, -98) * mm});
            skLineSegment(sketch, "E2.14.13.4", {"start": v(114.5, -83.5) * mm, "end": v(100, -83.5) * mm});
            skPoint(sketch, "E2.14.14.0", {"position": v(107.25, -107.25) * mm});
            skLineSegment(sketch, "E2.14.14.1", {"start": v(100, -100) * mm, "end": v(100, -114.5) * mm});
            skLineSegment(sketch, "E2.14.14.2", {"start": v(114.5, -100) * mm, "end": v(114.5, -114.5) * mm});
            skLineSegment(sketch, "E2.14.14.3", {"start": v(114.5, -114.5) * mm, "end": v(100, -114.5) * mm});
            skLineSegment(sketch, "E2.14.14.4", {"start": v(114.5, -100) * mm, "end": v(100, -100) * mm});
            skPoint(sketch, "E2.14.15.0", {"position": v(107.25, -123.75) * mm});
            skLineSegment(sketch, "E2.14.15.1", {"start": v(100, -116.5) * mm, "end": v(100, -131) * mm});
            skLineSegment(sketch, "E2.14.15.2", {"start": v(114.5, -116.5) * mm, "end": v(114.5, -131) * mm});
            skLineSegment(sketch, "E2.14.15.3", {"start": v(114.5, -131) * mm, "end": v(100, -131) * mm});
            skLineSegment(sketch, "E2.14.15.4", {"start": v(114.5, -116.5) * mm, "end": v(100, -116.5) * mm});
            skPoint(sketch, "E2.15.0.0", {"position": v(123.75, 123.75) * mm});
            skLineSegment(sketch, "E2.15.0.1", {"start": v(116.5, 131) * mm, "end": v(116.5, 116.5) * mm});
            skLineSegment(sketch, "E2.15.0.2", {"start": v(131, 131) * mm, "end": v(131, 116.5) * mm});
            skLineSegment(sketch, "E2.15.0.3", {"start": v(131, 116.5) * mm, "end": v(116.5, 116.5) * mm});
            skLineSegment(sketch, "E2.15.0.4", {"start": v(131, 131) * mm, "end": v(116.5, 131) * mm});
            skPoint(sketch, "E2.15.1.0", {"position": v(123.75, 107.25) * mm});
            skLineSegment(sketch, "E2.15.1.1", {"start": v(116.5, 114.5) * mm, "end": v(116.5, 100) * mm});
            skLineSegment(sketch, "E2.15.1.2", {"start": v(131, 114.5) * mm, "end": v(131, 100) * mm});
            skLineSegment(sketch, "E2.15.1.3", {"start": v(131, 100) * mm, "end": v(116.5, 100) * mm});
            skLineSegment(sketch, "E2.15.1.4", {"start": v(131, 114.5) * mm, "end": v(116.5, 114.5) * mm});
            skPoint(sketch, "E2.15.2.0", {"position": v(123.75, 90.75) * mm});
            skLineSegment(sketch, "E2.15.2.1", {"start": v(116.5, 98) * mm, "end": v(116.5, 83.5) * mm});
            skLineSegment(sketch, "E2.15.2.2", {"start": v(131, 98) * mm, "end": v(131, 83.5) * mm});
            skLineSegment(sketch, "E2.15.2.3", {"start": v(131, 83.5) * mm, "end": v(116.5, 83.5) * mm});
            skLineSegment(sketch, "E2.15.2.4", {"start": v(131, 98) * mm, "end": v(116.5, 98) * mm});
            skPoint(sketch, "E2.15.3.0", {"position": v(123.75, 74.25) * mm});
            skLineSegment(sketch, "E2.15.3.1", {"start": v(116.5, 81.5) * mm, "end": v(116.5, 67) * mm});
            skLineSegment(sketch, "E2.15.3.2", {"start": v(131, 81.5) * mm, "end": v(131, 67) * mm});
            skLineSegment(sketch, "E2.15.3.3", {"start": v(131, 67) * mm, "end": v(116.5, 67) * mm});
            skLineSegment(sketch, "E2.15.3.4", {"start": v(131, 81.5) * mm, "end": v(116.5, 81.5) * mm});
            skPoint(sketch, "E2.15.4.0", {"position": v(123.75, 57.75) * mm});
            skLineSegment(sketch, "E2.15.4.1", {"start": v(116.5, 65) * mm, "end": v(116.5, 50.5) * mm});
            skLineSegment(sketch, "E2.15.4.2", {"start": v(131, 65) * mm, "end": v(131, 50.5) * mm});
            skLineSegment(sketch, "E2.15.4.3", {"start": v(131, 50.5) * mm, "end": v(116.5, 50.5) * mm});
            skLineSegment(sketch, "E2.15.4.4", {"start": v(131, 65) * mm, "end": v(116.5, 65) * mm});
            skPoint(sketch, "E2.15.5.0", {"position": v(123.75, 41.25) * mm});
            skLineSegment(sketch, "E2.15.5.1", {"start": v(116.5, 48.5) * mm, "end": v(116.5, 34) * mm});
            skLineSegment(sketch, "E2.15.5.2", {"start": v(131, 48.5) * mm, "end": v(131, 34) * mm});
            skLineSegment(sketch, "E2.15.5.3", {"start": v(131, 34) * mm, "end": v(116.5, 34) * mm});
            skLineSegment(sketch, "E2.15.5.4", {"start": v(131, 48.5) * mm, "end": v(116.5, 48.5) * mm});
            skPoint(sketch, "E2.15.6.0", {"position": v(123.75, 24.75) * mm});
            skLineSegment(sketch, "E2.15.6.1", {"start": v(116.5, 32) * mm, "end": v(116.5, 17.5) * mm});
            skLineSegment(sketch, "E2.15.6.2", {"start": v(131, 32) * mm, "end": v(131, 17.5) * mm});
            skLineSegment(sketch, "E2.15.6.3", {"start": v(131, 17.5) * mm, "end": v(116.5, 17.5) * mm});
            skLineSegment(sketch, "E2.15.6.4", {"start": v(131, 32) * mm, "end": v(116.5, 32) * mm});
            skPoint(sketch, "E2.15.7.0", {"position": v(123.75, 8.25) * mm});
            skLineSegment(sketch, "E2.15.7.1", {"start": v(116.5, 15.5) * mm, "end": v(116.5, 1) * mm});
            skLineSegment(sketch, "E2.15.7.2", {"start": v(131, 15.5) * mm, "end": v(131, 1) * mm});
            skLineSegment(sketch, "E2.15.7.3", {"start": v(131, 1) * mm, "end": v(116.5, 1) * mm});
            skLineSegment(sketch, "E2.15.7.4", {"start": v(131, 15.5) * mm, "end": v(116.5, 15.5) * mm});
            skPoint(sketch, "E2.15.8.0", {"position": v(123.75, -8.25) * mm});
            skLineSegment(sketch, "E2.15.8.1", {"start": v(116.5, -1) * mm, "end": v(116.5, -15.5) * mm});
            skLineSegment(sketch, "E2.15.8.2", {"start": v(131, -1) * mm, "end": v(131, -15.5) * mm});
            skLineSegment(sketch, "E2.15.8.3", {"start": v(131, -15.5) * mm, "end": v(116.5, -15.5) * mm});
            skLineSegment(sketch, "E2.15.8.4", {"start": v(131, -1) * mm, "end": v(116.5, -1) * mm});
            skPoint(sketch, "E2.15.9.0", {"position": v(123.75, -24.75) * mm});
            skLineSegment(sketch, "E2.15.9.1", {"start": v(116.5, -17.5) * mm, "end": v(116.5, -32) * mm});
            skLineSegment(sketch, "E2.15.9.2", {"start": v(131, -17.5) * mm, "end": v(131, -32) * mm});
            skLineSegment(sketch, "E2.15.9.3", {"start": v(131, -32) * mm, "end": v(116.5, -32) * mm});
            skLineSegment(sketch, "E2.15.9.4", {"start": v(131, -17.5) * mm, "end": v(116.5, -17.5) * mm});
            skPoint(sketch, "E2.15.10.0", {"position": v(123.75, -41.25) * mm});
            skLineSegment(sketch, "E2.15.10.1", {"start": v(116.5, -34) * mm, "end": v(116.5, -48.5) * mm});
            skLineSegment(sketch, "E2.15.10.2", {"start": v(131, -34) * mm, "end": v(131, -48.5) * mm});
            skLineSegment(sketch, "E2.15.10.3", {"start": v(131, -48.5) * mm, "end": v(116.5, -48.5) * mm});
            skLineSegment(sketch, "E2.15.10.4", {"start": v(131, -34) * mm, "end": v(116.5, -34) * mm});
            skPoint(sketch, "E2.15.11.0", {"position": v(123.75, -57.75) * mm});
            skLineSegment(sketch, "E2.15.11.1", {"start": v(116.5, -50.5) * mm, "end": v(116.5, -65) * mm});
            skLineSegment(sketch, "E2.15.11.2", {"start": v(131, -50.5) * mm, "end": v(131, -65) * mm});
            skLineSegment(sketch, "E2.15.11.3", {"start": v(131, -65) * mm, "end": v(116.5, -65) * mm});
            skLineSegment(sketch, "E2.15.11.4", {"start": v(131, -50.5) * mm, "end": v(116.5, -50.5) * mm});
            skPoint(sketch, "E2.15.12.0", {"position": v(123.75, -74.25) * mm});
            skLineSegment(sketch, "E2.15.12.1", {"start": v(116.5, -67) * mm, "end": v(116.5, -81.5) * mm});
            skLineSegment(sketch, "E2.15.12.2", {"start": v(131, -67) * mm, "end": v(131, -81.5) * mm});
            skLineSegment(sketch, "E2.15.12.3", {"start": v(131, -81.5) * mm, "end": v(116.5, -81.5) * mm});
            skLineSegment(sketch, "E2.15.12.4", {"start": v(131, -67) * mm, "end": v(116.5, -67) * mm});
            skPoint(sketch, "E2.15.13.0", {"position": v(123.75, -90.75) * mm});
            skLineSegment(sketch, "E2.15.13.1", {"start": v(116.5, -83.5) * mm, "end": v(116.5, -98) * mm});
            skLineSegment(sketch, "E2.15.13.2", {"start": v(131, -83.5) * mm, "end": v(131, -98) * mm});
            skLineSegment(sketch, "E2.15.13.3", {"start": v(131, -98) * mm, "end": v(116.5, -98) * mm});
            skLineSegment(sketch, "E2.15.13.4", {"start": v(131, -83.5) * mm, "end": v(116.5, -83.5) * mm});
            skPoint(sketch, "E2.15.14.0", {"position": v(123.75, -107.25) * mm});
            skLineSegment(sketch, "E2.15.14.1", {"start": v(116.5, -100) * mm, "end": v(116.5, -114.5) * mm});
            skLineSegment(sketch, "E2.15.14.2", {"start": v(131, -100) * mm, "end": v(131, -114.5) * mm});
            skLineSegment(sketch, "E2.15.14.3", {"start": v(131, -114.5) * mm, "end": v(116.5, -114.5) * mm});
            skLineSegment(sketch, "E2.15.14.4", {"start": v(131, -100) * mm, "end": v(116.5, -100) * mm});
            skPoint(sketch, "E2.15.15.0", {"position": v(123.75, -123.75) * mm});
            skLineSegment(sketch, "E2.15.15.1", {"start": v(116.5, -116.5) * mm, "end": v(116.5, -131) * mm});
            skLineSegment(sketch, "E2.15.15.2", {"start": v(131, -116.5) * mm, "end": v(131, -131) * mm});
            skLineSegment(sketch, "E2.15.15.3", {"start": v(131, -131) * mm, "end": v(116.5, -131) * mm});
            skLineSegment(sketch, "E2.15.15.4", {"start": v(131, -116.5) * mm, "end": v(116.5, -116.5) * mm});
            skLineSegment(sketch, "E2.direction1", {"start": v(-131, 116.5) * mm, "end": v(-114.5, 116.5) * mm, "construction": true});
            skLineSegment(sketch, "E2.direction2", {"start": v(-131, 116.5) * mm, "end": v(-131, 100) * mm, "construction": true});
            skSolve(sketch);
        }
        {
            var Q0;
            Q0 = qSketchRegion(id + "F0", true);
            extrude(context, id + "F2", {"entities" : qUnion([Q0]), "oppositeDirection" : true, "depth" : 2 * mm});
        }
        {
            var Q0;
            Q0 = qSketchRegion(id + "F1", true);
            extrude(context, id + "F3", {"entities" : qUnion([Q0]), "operationType" : NewBodyOperationType.ADD, "depth" : 2 * mm});
        }
    });
